FCSTD DOCUMENT  (FreeCAD 0.20R29177 +426 (Git))
Label: gearbox_00
License: Other
LicenseURL: https://www.gnu.org/licenses/gpl-3.0.en.html
objects: Part::Cylinder×128, Part::Feature×75, Part::MultiFuse×58, Part::Box×44, Part::Cut×41, Part::Chamfer×20, App::DocumentObjectGroup×9, Part::MultiCommon×7, Part::Fillet×6, Part::Part2DObjectPython×5, Part::Cone×4, Part::RegularPolygon×4, Part::Extrusion×4, Part::Compound×2
note: 398 computed .brp shape members not serialized (recipe doc carries the construction recipe); baked Part::Feature solids carry a one-line shape summary decoded from their .brp

FEATURE [Part::Box] Box377  label="Cube"
  AttacherType = Attacher::AttachEngine3D
  Height = 51
  Length = 8
  Placement = pos=(207,-16,35) rot=(0,0,1;0rad)
  Width = 32
FEATURE [Part::Box] Box761  label="Cube"
  AttacherType = Attacher::AttachEngine3D
  Height = 16
  Length = 1.5
  Placement = pos=(213,-16.25,47) rot=(0,0,1;0rad)
  Width = 10
FEATURE [Part::Box] Box762  label="Cube"
  AttacherType = Attacher::AttachEngine3D
  Height = 16
  Length = 1.5
  Placement = pos=(213,6.25,47) rot=(0,0,1;0rad)
  Width = 10
FEATURE [Part::Cylinder] Cylinder1492202  label="Cylinder"
  Angle = 360
  AttacherType = Attacher::AttachEngine3D
  FirstAngle = 0
  Height = 15.5
  Placement = pos=(199,0,55) rot=(0,1,0;1.5708rad)
  Radius = 3
  SecondAngle = 0
FEATURE [Part::Cylinder] Cylinder1492203  label="Cylinder"
  Angle = 360
  AttacherType = Attacher::AttachEngine3D
  FirstAngle = 0
  Height = 3.1
  Placement = pos=(211.4,0,55) rot=(0,1,0;1.5708rad)
  Radius = 4.6
  SecondAngle = 0
FEATURE [Part::Cylinder] Cylinder1492204  label="Cylinder"
  Angle = 360
  AttacherType = Attacher::AttachEngine3D
  FirstAngle = 0
  Height = 3.1
  Placement = pos=(206.4,0,55) rot=(0,1,0;1.5708rad)
  Radius = 4.6
  SecondAngle = 0
FEATURE [Part::Cylinder] Cylinder1492234  label="Cylinder"
  Angle = 360
  AttacherType = Attacher::AttachEngine3D
  FirstAngle = 0
  Height = 16
  Placement = pos=(211,-21,66) rot=(-1,0,0;1.5708rad)
  Radius = 1.25
  SecondAngle = 0
FEATURE [Part::Cylinder] Cylinder1492235  label="Cylinder"
  Angle = 360
  AttacherType = Attacher::AttachEngine3D
  FirstAngle = 0
  Height = 16
  Placement = pos=(211,-21,43) rot=(-1,0,0;1.5708rad)
  Radius = 1.25
  SecondAngle = 0
FEATURE [Part::Cylinder] Cylinder1492236  label="Cylinder"
  Angle = 360
  AttacherType = Attacher::AttachEngine3D
  FirstAngle = 0
  Height = 16
  Placement = pos=(211,-21,82) rot=(-1,0,0;1.5708rad)
  Radius = 1.25
  SecondAngle = 0
FEATURE [Part::Cylinder] Cylinder1492237  label="Cylinder"
  Angle = 360
  AttacherType = Attacher::AttachEngine3D
  FirstAngle = 0
  Height = 16
  Placement = pos=(211,5,66) rot=(-1,0,0;1.5708rad)
  Radius = 1.25
  SecondAngle = 0
FEATURE [Part::Cylinder] Cylinder1492238  label="Cylinder"
  Angle = 360
  AttacherType = Attacher::AttachEngine3D
  FirstAngle = 0
  Height = 16
  Placement = pos=(211,5,43) rot=(-1,0,0;1.5708rad)
  Radius = 1.25
  SecondAngle = 0
FEATURE [Part::Cylinder] Cylinder1492239  label="Cylinder"
  Angle = 360
  AttacherType = Attacher::AttachEngine3D
  FirstAngle = 0
  Height = 16
  Placement = pos=(211,5,82) rot=(-1,0,0;1.5708rad)
  Radius = 1.25
  SecondAngle = 0
FEATURE [Part::Cylinder] Cylinder1492270  label="Cylinder"
  Angle = 360
  AttacherType = Attacher::AttachEngine3D
  FirstAngle = 0
  Height = 10
  Placement = pos=(206,11.5,40) rot=(0,1,0;1.5708rad)
  Radius = 1.25
  SecondAngle = 0
FEATURE [Part::Cylinder] Cylinder1492272  label="Cylinder"
  Angle = 360
  AttacherType = Attacher::AttachEngine3D
  FirstAngle = 0
  Height = 10
  Placement = pos=(206,-11.5,40) rot=(0,1,0;1.5708rad)
  Radius = 1.25
  SecondAngle = 0
FEATURE [Part::Cylinder] Cylinder1492273  label="Cylinder"
  Angle = 360
  AttacherType = Attacher::AttachEngine3D
  FirstAngle = 0
  Height = 10
  Placement = pos=(206,-3,76) rot=(0,1,0;1.5708rad)
  Radius = 1.25
  SecondAngle = 0
FEATURE [Part::MultiFuse] Fusion004002009002027014004009002002008002004029002015013017006002012002031033002013006007008014029072011018024002019049062029014012006016002033001057009078004002010025  label="Fusion"
  Placement = pos=(0.5,0,0) rot=(0,0,1;0rad)
  Refine = true
  Shapes = -> [Cylinder1492202,Cylinder1492203,Cylinder1492204]
FEATURE [Part::Cut] Cut176013009033007019019008010045003002004008006021005004004004004002012033009016002012007022024055  label="Cut"
  Base = -> Box377
  Refine = true
  Tool = -> Fusion004002009002027014004009002002008002004029002015013017006002012002031033002013006007008014029072011018024002019049062029014012006016002033001057009078004002010025
FEATURE [Part::MultiFuse] Fusion004002009002027014004009002002008002004029002015013017006002012002031033002013006007008014029072011018024002019049062029014012006016002033001057009078004002010031010  label="Fusion"
  Placement = pos=(0.5,0,0) rot=(0,0,1;0rad)
  Refine = true
  Shapes = -> [Box762,Box761]
FEATURE [Part::Cut] Cut176013009033007019019008010045003002004008006021005004004004004002012033009016002012007022024056  label="Cut"
  Base = -> Cut176013009033007019019008010045003002004008006021005004004004004002012033009016002012007022024055
  Refine = true
  Tool = -> Fusion004002009002027014004009002002008002004029002015013017006002012002031033002013006007008014029072011018024002019049062029014012006016002033001057009078004002010031010
FEATURE [Part::MultiFuse] Fusion004002009002027014004009002002008002004029002015013017006002012002031033002013006007008014029072011018024002019049062029014012006016002033001057009078004002010031012  label="Fusion"
  Refine = true
  Shapes = -> [Cylinder1492234,Cylinder1492235,Cylinder1492236,Cylinder1492237,Cylinder1492238,Cylinder1492239]
FEATURE [Part::Cut] Cut176013009033007019019008010045003002004008006021005004004004004002012033009016002012007022024057  label="Cut"
  Base = -> Cut176013009033007019019008010045003002004008006021005004004004004002012033009016002012007022024056
  Refine = true
  Tool = -> Fusion004002009002027014004009002002008002004029002015013017006002012002031033002013006007008014029072011018024002019049062029014012006016002033001057009078004002010031012
FEATURE [Part::MultiFuse] Fusion004002009002027014004009002002008002004029002015013017006002012002031033002013006007008014029072011018024002019049062029014012006016002033001057009078004002010031016012003006  label="Fusion"
  Refine = true
  Shapes = -> [Cylinder1492270,Cylinder1492272,Cylinder1492273]
FEATURE [Part::Cut] Cut176013009033007019019008010045003002004008006010017027003005053020098001031003007007002011005005004026009003003  label="Cut"
  Base = -> Cut176013009033007019019008010045003002004008006021005004004004004002012033009016002012007022024057
  Refine = true
  Tool = -> Fusion004002009002027014004009002002008002004029002015013017006002012002031033002013006007008014029072011018024002019049062029014012006016002033001057009078004002010031016012003006
FEATURE [Part::Feature] Part__Mirroring007002003002018002002002005004004002003004003003004003001  label="diff-front-side-right-ALU5mm"
  shape: bbox 75 x 5 x 51 mm, 32 faces (baked)
FEATURE [Part::Feature] Cut176013009033007019019008010045003002004008006021005004004004004002012033009016002012007022024058001  label="diff-front-side-left-ALU5mm"
  shape: bbox 75 x 5 x 51 mm, 32 faces (baked)
FEATURE [Part::Feature] Compound003001  label="Joint"
  Placement = pos=(36,0,0) rot=(0,0,1;0rad)
  shape: bbox 25.01 x 11 x 13.99 mm, 52 faces, 2 solids (baked)
FEATURE [Part::Feature] Compound003002001  label="Joint"
  Placement = pos=(70,0,9) rot=(0,0,1;0rad)
  shape: bbox 25.01 x 11 x 13.92 mm, 52 faces, 2 solids (baked)
FEATURE [Part::Cone] Cone003  label="Cone"
  Angle = 360
  AttacherType = Attacher::AttachEngine3D
  Height = 1.5
  Placement = pos=(205.5,0,48) rot=(0,1,0;1.5708rad)
  Radius1 = 1
  Radius2 = 1.9
FEATURE [Part::Cone] Cone004  label="Cone"
  Angle = 360
  AttacherType = Attacher::AttachEngine3D
  Height = 1.5
  Placement = pos=(205.5,0,62) rot=(0,1,0;1.5708rad)
  Radius1 = 1
  Radius2 = 1.9
FEATURE [Part::Cone] Cone005  label="Cone"
  Angle = 360
  AttacherType = Attacher::AttachEngine3D
  Height = 1.5
  Placement = pos=(205.5,7,55) rot=(0,1,0;1.5708rad)
  Radius1 = 1
  Radius2 = 1.9
FEATURE [Part::Cone] Cone006  label="Cone"
  Angle = 360
  AttacherType = Attacher::AttachEngine3D
  Height = 1.5
  Placement = pos=(205.5,-7,55) rot=(0,1,0;1.5708rad)
  Radius1 = 1
  Radius2 = 1.9
FEATURE [Part::Feature] Cut176013009033007019019008010045003002004008006010017027003005053020098001031003007007002011005005004026009003002  label="BEARING-17x23x4-6703"
  Placement = pos=(264,-75,9) rot=(0,0,1;1.5708rad)
  shape: bbox 4 x 23 x 23 mm, 4 faces (baked)
FEATURE [Part::Feature] Cut176013009033007019019008010045003002004008006021005004004004004002012033009016002012007022024086  label="BEARING-5x8x2.5-MR85ZZ"
  Placement = pos=(273.5,-62,25.5) rot=(0,0,1;1.5708rad)
  shape: bbox 2.5 x 8 x 8 mm, 4 faces (baked)
FEATURE [Part::Cylinder] Cylinder1051  label="Cylinder"
  Angle = 360
  AttacherType = Attacher::AttachEngine3D
  FirstAngle = 0
  Height = 22
  Placement = pos=(118.375,0,47.903) rot=(0,1,0;1.309rad)
  Radius = 4
  SecondAngle = 0
FEATURE [Part::Cylinder] Cylinder1492252  label="Cylinder"
  Angle = 360
  AttacherType = Attacher::AttachEngine3D
  FirstAngle = 0
  Height = 10
  Placement = pos=(198,0,55) rot=(0,1,0;1.5708rad)
  Radius = 5
  SecondAngle = 0
FEATURE [Part::Cylinder] Cylinder1492253  label="Cylinder"
  Angle = 360
  AttacherType = Attacher::AttachEngine3D
  FirstAngle = 0
  Height = 48
  Placement = pos=(152,0,55) rot=(0,1,0;1.5708rad)
  Radius = 2.5
  SecondAngle = 0
FEATURE [Part::Cylinder] Cylinder1492268  label="motor"
  Angle = 360
  AttacherType = Attacher::AttachEngine3D
  FirstAngle = 0
  Height = 60
  Placement = pos=(131.5,14,77) rot=(0,1,0;1.5708rad)
  Radius = 12.5
  SecondAngle = 0
FEATURE [Part::Cylinder] Cylinder1492269  label="motor-axle"
  Angle = 360
  AttacherType = Attacher::AttachEngine3D
  FirstAngle = 0
  Height = 53
  Placement = pos=(154.5,14,77) rot=(0,1,0;1.5708rad)
  Radius = 2
  SecondAngle = 0
FEATURE [Part::Cylinder] Cylinder1492276  label="Cylinder"
  Angle = 360
  AttacherType = Attacher::AttachEngine3D
  FirstAngle = 0
  Height = 2
  Placement = pos=(205,0,55) rot=(0,1,0;1.5708rad)
  Radius = 15.5
  SecondAngle = 0
FEATURE [Part::Cylinder] Cylinder1492278  label="Cylinder"
  Angle = 360
  AttacherType = Attacher::AttachEngine3D
  FirstAngle = 0
  Height = 2
  Placement = pos=(199,0,55) rot=(0,1,0;1.5708rad)
  Radius = 11
  SecondAngle = 0
FEATURE [Part::Cylinder] Cylinder1492279  label="Cylinder"
  Angle = 360
  AttacherType = Attacher::AttachEngine3D
  FirstAngle = 0
  Height = 8
  Placement = pos=(199,0,62) rot=(0,1,0;1.5708rad)
  Radius = 1
  SecondAngle = 0
FEATURE [Part::Cylinder] Cylinder1492280  label="Cylinder"
  Angle = 360
  AttacherType = Attacher::AttachEngine3D
  FirstAngle = 0
  Height = 8
  Placement = pos=(199,0,48) rot=(0,1,0;1.5708rad)
  Radius = 1
  SecondAngle = 0
FEATURE [Part::Cylinder] Cylinder1492281  label="Cylinder"
  Angle = 360
  AttacherType = Attacher::AttachEngine3D
  FirstAngle = 0
  Height = 8
  Placement = pos=(199,7,55) rot=(0,1,0;1.5708rad)
  Radius = 1
  SecondAngle = 0
FEATURE [Part::Cylinder] Cylinder1492282  label="Cylinder"
  Angle = 360
  AttacherType = Attacher::AttachEngine3D
  FirstAngle = 0
  Height = 8
  Placement = pos=(199,-7,55) rot=(0,1,0;1.5708rad)
  Radius = 1
  SecondAngle = 0
FEATURE [Part::MultiFuse] Fusion004002009002027014004009002002008002004029002015013017006002012002031033002013006007008014029072011018024002019049062029014012006016002033001057009078004002010031016012003011  label="Fusion"
  Refine = true
  Shapes = -> [Cylinder1492279,Cylinder1492280,Cylinder1492281,Cylinder1492282,Cone003,Cone004,Cone005,Cone006]
FEATURE [Part::MultiFuse] Fusion088026007031024007008004100051055007010008005020006  label="rear-prop-shaft-STEEL"
  Refine = true
  Shapes = -> [Compound003002001,Compound003001,Cylinder1051]
FEATURE [Part::Feature] Transmission_Gear_12T_pitch214001_solid  label="Transmission_Gear_12T_pitch214"
  Placement = pos=(205,14,77) rot=(0,0,1;0rad)
  shape: bbox 10 x 16.64 x 16.64 mm, 740 faces (baked)
FEATURE [Part::MultiFuse] Fusion004002009002027014004009002002008002004029002015013017006002012002031033002013006007008014029072011018024002019049062029014012006016002033001057009078004002010031016012003004  label="GEARMOTOR"
  Placement = pos=(-0.5,-1,-5.5) rot=(0,0,1;0rad)
  Refine = true
  Shapes = -> [Cylinder1492268,Cylinder1492269,Transmission_Gear_12T_pitch214001_solid]
FEATURE [Part::Feature] Transmission_Gear_24T_pitch214001_solid  label="Transmission_Gear_24T_pitch214001 (Solid)"
  Placement = pos=(199,0,55) rot=(0,0,1;0rad)
  shape: bbox 8 x 30.9 x 30.9 mm, 1340 faces (baked)
FEATURE [Part::MultiFuse] Fusion004002009002027014004009002002008002004029002015013017006002012002031033002013006007008014029072011018024002019049062029014012006016002033001057009078004002010031016012003007  label="Fusion"
  Refine = true
  Shapes = -> [Cylinder1492276,Transmission_Gear_24T_pitch214001_solid]
FEATURE [Part::Cut] Cut176013009033007019019008010045003002004008006010017027003005053020098001031003007007002011005005004026009003004  label="Cut"
  Base = -> Fusion004002009002027014004009002002008002004029002015013017006002012002031033002013006007008014029072011018024002019049062029014012006016002033001057009078004002010031016012003007
  Refine = true
  Tool = -> Cylinder1492278
FEATURE [Part::Cut] Cut176013009033007019019008010045003002004008006010017027003005053020098001031003007007002011005005004026009003005  label="Cut"
  Base = -> Cut176013009033007019019008010045003002004008006010017027003005053020098001031003007007002011005005004026009003004
  Refine = true
  Tool = -> Cylinder1492252
FEATURE [Part::Cut] Cut176013009033007019019008010045003002004008006010017027003005053020098001031003007007002011005005004026009003009  label="gearbox-gear"
  Base = -> Cut176013009033007019019008010045003002004008006010017027003005053020098001031003007007002011005005004026009003005
  Refine = true
  Tool = -> Fusion004002009002027014004009002002008002004029002015013017006002012002031033002013006007008014029072011018024002019049062029014012006016002033001057009078004002010031016012003011
FEATURE [Part::Cylinder] Cylinder1492283  label="Cylinder"
  Angle = 360
  AttacherType = Attacher::AttachEngine3D
  FirstAngle = 0
  Height = 8
  Placement = pos=(199,0,55) rot=(0,1,0;1.5708rad)
  Radius = 5
  SecondAngle = 0
FEATURE [Part::Cylinder] Cylinder1492284  label="Cylinder"
  Angle = 360
  AttacherType = Attacher::AttachEngine3D
  FirstAngle = 0
  Height = 2
  Placement = pos=(199,0,55) rot=(0,1,0;1.5708rad)
  Radius = 11
  SecondAngle = 0
FEATURE [Part::Cylinder] Cylinder1492285  label="Cylinder"
  Angle = 360
  AttacherType = Attacher::AttachEngine3D
  FirstAngle = 0
  Height = 8
  Placement = pos=(191,0,55) rot=(0,1,0;1.5708rad)
  Radius = 8.5
  SecondAngle = 0
FEATURE [Part::Cylinder] Cylinder1492286  label="Cylinder"
  Angle = 360
  AttacherType = Attacher::AttachEngine3D
  FirstAngle = 0
  Height = 16
  Placement = pos=(191,0,55) rot=(0,1,0;1.5708rad)
  Radius = 2.5
  SecondAngle = 0
FEATURE [Part::Cylinder] Cylinder1492287  label="Cylinder"
  Angle = 360
  AttacherType = Attacher::AttachEngine3D
  FirstAngle = 0
  Height = 12
  Placement = pos=(204.5,0,49) rot=(0,1,0;0rad)
  Radius = 1
  SecondAngle = 0
FEATURE [Part::Cylinder] Cylinder1492288  label="Cylinder"
  Angle = 360
  AttacherType = Attacher::AttachEngine3D
  FirstAngle = 0
  Height = 12
  Placement = pos=(198,0,62) rot=(0,1,0;1.5708rad)
  Radius = 0.9
  SecondAngle = 0
FEATURE [Part::Cylinder] Cylinder1492289  label="Cylinder"
  Angle = 360
  AttacherType = Attacher::AttachEngine3D
  FirstAngle = 0
  Height = 12
  Placement = pos=(198,0,48) rot=(0,1,0;1.5708rad)
  Radius = 0.9
  SecondAngle = 0
FEATURE [Part::Cylinder] Cylinder1492290  label="Cylinder"
  Angle = 360
  AttacherType = Attacher::AttachEngine3D
  FirstAngle = 0
  Height = 12
  Placement = pos=(198,7,55) rot=(0,1,0;1.5708rad)
  Radius = 0.9
  SecondAngle = 0
FEATURE [Part::Cylinder] Cylinder1492291  label="Cylinder"
  Angle = 360
  AttacherType = Attacher::AttachEngine3D
  FirstAngle = 0
  Height = 12
  Placement = pos=(198,-7,55) rot=(0,1,0;1.5708rad)
  Radius = 0.9
  SecondAngle = 0
FEATURE [Part::Cylinder] Cylinder1492292  label="Cylinder"
  Angle = 360
  AttacherType = Attacher::AttachEngine3D
  FirstAngle = 0
  Height = 3
  Radius = 5.75
  SecondAngle = 0
FEATURE [Part::Cylinder] Cylinder1492293  label="Cylinder"
  Angle = 30
  AttacherType = Attacher::AttachEngine3D
  FirstAngle = 0
  Height = 3
  Placement = pos=(0,0,0) rot=(0,0,1;0.523599rad)
  Radius = 5.75
  SecondAngle = 0
FEATURE [Part::Cylinder] Cylinder1492294  label="Cylinder"
  Angle = 30
  AttacherType = Attacher::AttachEngine3D
  FirstAngle = 0
  Height = 3
  Placement = pos=(0,0,0) rot=(0,0,1;3.66519rad)
  Radius = 5.75
  SecondAngle = 0
FEATURE [Part::Cylinder] Cylinder1492295  label="Cylinder"
  Angle = 360
  AttacherType = Attacher::AttachEngine3D
  FirstAngle = 0
  Height = 3
  Radius = 5.75
  SecondAngle = 0
FEATURE [Part::Cylinder] Cylinder1492296  label="Cylinder"
  Angle = 40
  AttacherType = Attacher::AttachEngine3D
  FirstAngle = 0
  Height = 3
  Placement = pos=(0,0,0) rot=(0,0,1;0.523599rad)
  Radius = 5.75
  SecondAngle = 0
FEATURE [Part::Cylinder] Cylinder1492297  label="Cylinder"
  Angle = 40
  AttacherType = Attacher::AttachEngine3D
  FirstAngle = 0
  Height = 3
  Placement = pos=(0,0,0) rot=(0,0,1;3.66519rad)
  Radius = 5.75
  SecondAngle = 0
FEATURE [Part::Cylinder] Cylinder1492298  label="Cylinder"
  Angle = 360
  AttacherType = Attacher::AttachEngine3D
  FirstAngle = 0
  Height = 11
  Radius = 2.5
  SecondAngle = 0
FEATURE [Part::Cylinder] Cylinder1492299  label="Cylinder"
  Angle = 360
  AttacherType = Attacher::AttachEngine3D
  FirstAngle = 0
  Height = 3
  Placement = pos=(191,0,55) rot=(0,1,0;1.5708rad)
  Radius = 3
  SecondAngle = 0
FEATURE [Part::MultiFuse] Fusion004002009002027014004009002002008002004029002015013017006002012002031033002013006007008014029072011018024002019049062029014012006016002033001057009078004002010031016012003009  label="Fusion"
  Refine = true
  Shapes = -> [Cylinder1492285,Cylinder1492283,Cylinder1492284]
FEATURE [Part::Cut] Cut176013009033007019019008010045003002004008006010017027003005053020098001031003007007002011005005004026009003007  label="Cut"
  Base = -> Fusion004002009002027014004009002002008002004029002015013017006002012002031033002013006007008014029072011018024002019049062029014012006016002033001057009078004002010031016012003009
  Refine = true
  Tool = -> Cylinder1492286
FEATURE [Part::Cut] Cut176013009033007019019008010045003002004008006010017027003005053020098001031003007007002011005005004026009003008  label="Cut"
  Base = -> Cut176013009033007019019008010045003002004008006010017027003005053020098001031003007007002011005005004026009003007
  Refine = true
  Tool = -> Cylinder1492287
FEATURE [Part::MultiFuse] Fusion004002009002027014004009002002008002004029002015013017006002012002031033002013006007008014029072011018024002019049062029014012006016002033001057009078004002010031016012003010  label="Fusion"
  Placement = pos=(-3,0,0) rot=(0,0,1;0rad)
  Refine = true
  Shapes = -> [Cylinder1492288,Cylinder1492289,Cylinder1492290,Cylinder1492291]
FEATURE [Part::Cut] Cut176013009033007019019008010045003002004008006010017027003005053020098001031003007007002011005005004026009003010  label="Cut"
  Base = -> Cut176013009033007019019008010045003002004008006010017027003005053020098001031003007007002011005005004026009003008
  Refine = true
  Tool = -> Fusion004002009002027014004009002002008002004029002015013017006002012002031033002013006007008014029072011018024002019049062029014012006016002033001057009078004002010031016012003010
FEATURE [Part::MultiFuse] Fusion004002009002027014004009002002008002004029002015013017006002012002031033002013006007008014029072011018024002019049062029014012006016002033001057009078004002010031016012003012  label="Fusion"
  Refine = true
  Shapes = -> [Cylinder1492293,Cylinder1492294]
FEATURE [Part::Cut] Cut176013009033007019019008010045003002004008006010017027003005053020098001031003007007002011005005004026009003011  label="Cut"
  Base = -> Cylinder1492292
  Placement = pos=(191,0,55) rot=(0,1,0;1.5708rad)
  Refine = true
  Tool = -> Fusion004002009002027014004009002002008002004029002015013017006002012002031033002013006007008014029072011018024002019049062029014012006016002033001057009078004002010031016012003012
FEATURE [Part::Cut] Cut176013009033007019019008010045003002004008006010017027003005053020098001031003007007002011005005004026009003016  label="Cut"
  Base = -> Cut176013009033007019019008010045003002004008006010017027003005053020098001031003007007002011005005004026009003010
  Refine = true
  Tool = -> Cut176013009033007019019008010045003002004008006010017027003005053020098001031003007007002011005005004026009003011
FEATURE [Part::Cut] Cut176013009033007019019008010045003002004008006010017027003005053020098001031003007007002011005005004026009003017  label="gearbox-gear-lock-BRASS"
  Base = -> Cut176013009033007019019008010045003002004008006010017027003005053020098001031003007007002011005005004026009003016
  Refine = true
  Tool = -> Cylinder1492299
FEATURE [Part::MultiFuse] Fusion004002009002027014004009002002008002004029002015013017006002012002031033002013006007008014029072011018024002019049062029014012006016002033001057009078004002010031016012003013  label="Fusion"
  Refine = true
  Shapes = -> [Cylinder1492296,Cylinder1492297]
FEATURE [Part::Cut] Cut176013009033007019019008010045003002004008006010017027003005053020098001031003007007002011005005004026009003013  label="Cut"
  Base = -> Cylinder1492295
  Placement = pos=(0,0,0) rot=(0,0,1;0.174533rad)
  Refine = true
  Tool = -> Fusion004002009002027014004009002002008002004029002015013017006002012002031033002013006007008014029072011018024002019049062029014012006016002033001057009078004002010031016012003013
FEATURE [Part::RegularPolygon] RegularPolygon002  label="Regular polygon"
  AttacherType = Attacher::AttachEngine3D
  Circumradius = 5.75
  Polygon = 6
FEATURE [Part::Extrusion] Extrude007025
  Base = -> RegularPolygon002
  Dir = (0,0,1)
  DirMode = 2
  FaceMakerClass = Part::FaceMakerBullseye
  LengthFwd = 11
  LengthRev = 0
  Solid = true
  Symmetric = false
FEATURE [Part::Cut] Cut176013009033007019019008010045003002004008006010017027003005053020098001031003007007002011005005004026009003014  label="Cut"
  Base = -> Extrude007025
  Refine = true
  Tool = -> Cut176013009033007019019008010045003002004008006010017027003005053020098001031003007007002011005005004026009003013
FEATURE [Part::Cut] Cut176013009033007019019008010045003002004008006010017027003005053020098001031003007007002011005005004026009003015  label="Cut"
  Base = -> Cut176013009033007019019008010045003002004008006010017027003005053020098001031003007007002011005005004026009003014
  Placement = pos=(194,0,55) rot=(0,-1,0;1.5708rad)
  Refine = true
  Tool = -> Cylinder1492298
FEATURE [Part::Feature] Cut176013009033007019019008010045003002004008006021005004004004004002012033009016002012007007  label="BEARING-5x9x3-MR95ZZ"
  Placement = pos=(141,75,9) rot=(0,0,-1;1.5708rad)
  shape: bbox 3 x 9 x 9 mm, 4 faces (baked)
FEATURE [Part::Feature] Cut176013009033007019019008010045003002004008006021005004004004004002012033009016002012007006  label="BEARING-5x9x3-MR95ZZ"
  Placement = pos=(146,75,9) rot=(0,0,-1;1.5708rad)
  shape: bbox 3 x 9 x 9 mm, 4 faces (baked)
FEATURE [Part::Cylinder] Cylinder1492300  label="Cylinder"
  Angle = 360
  AttacherType = Attacher::AttachEngine3D
  FirstAngle = 0
  Height = 50
  Placement = pos=(157,11.5,40) rot=(0,1,0;1.5708rad)
  Radius = 1.5
  SecondAngle = 0
FEATURE [Part::Cylinder] Cylinder1492301  label="Cylinder"
  Angle = 360
  AttacherType = Attacher::AttachEngine3D
  FirstAngle = 0
  Height = 50
  Placement = pos=(157,-11.5,40) rot=(0,1,0;1.5708rad)
  Radius = 1.5
  SecondAngle = 0
FEATURE [Part::Cylinder] Cylinder1492302  label="Cylinder"
  Angle = 360
  AttacherType = Attacher::AttachEngine3D
  FirstAngle = 0
  Height = 50
  Placement = pos=(157,-3,76) rot=(0,1,0;1.5708rad)
  Radius = 1.5
  SecondAngle = 0
FEATURE [Part::Cylinder] Cylinder1492303  label="Cylinder"
  Angle = 360
  AttacherType = Attacher::AttachEngine3D
  FirstAngle = 0
  Height = 15
  Placement = pos=(179,0,55) rot=(0,1,0;1.5708rad)
  Radius = 3
  SecondAngle = 0
FEATURE [Part::MultiFuse] Fusion  label="gearbox-shaft-STEEL"
  Refine = true
  Shapes = -> [Cylinder1492303,Cylinder1492253]
FEATURE [Part::Cylinder] Cylinder1492304  label="Cylinder"
  Angle = 360
  AttacherType = Attacher::AttachEngine3D
  FirstAngle = 0
  Height = 2
  Placement = pos=(185.5,0,55) rot=(0,1,0;1.5708rad)
  Radius = 6
  SecondAngle = 0
FEATURE [Part::Cylinder] Cylinder1492305  label="Cylinder"
  Angle = 360
  AttacherType = Attacher::AttachEngine3D
  FirstAngle = 0
  Height = 2
  Placement = pos=(185.5,0,55) rot=(0,1,0;1.5708rad)
  Radius = 4.4
  SecondAngle = 0
FEATURE [Part::Cut] Cut
  Base = -> Cylinder1492304
  Refine = true
  Tool = -> Cylinder1492305
FEATURE [Part::Cut] Cut176013009033007019019008010045003002004008006010017027003005053020098001031003007007002011005005004026009004013003  label="gearbox-lock-STEEL"
  Base = -> Cut176013009033007019019008010045003002004008006010017027003005053020098001031003007007002011005005004026009003015
  Refine = true
  Tool = -> Cut
FEATURE [Part::Cylinder] Cylinder1492306  label="Cylinder"
  Angle = 360
  AttacherType = Attacher::AttachEngine3D
  FirstAngle = 0
  Height = 8
  Placement = pos=(207,0,55) rot=(0,-1,0;1.5708rad)
  Radius = 16
  SecondAngle = 0
FEATURE [Part::Cylinder] Cylinder1492308  label="Cylinder"
  Angle = 360
  AttacherType = Attacher::AttachEngine3D
  FirstAngle = 0
  Height = 50
  Placement = pos=(207,0,55) rot=(0,-1,0;1.5708rad)
  Radius = 4
  SecondAngle = 0
FEATURE [Part::Cylinder] Cylinder1492309  label="Cylinder"
  Angle = 360
  AttacherType = Attacher::AttachEngine3D
  FirstAngle = 0
  Height = 28
  Placement = pos=(207,0,55) rot=(0,-1,0;1.5708rad)
  Radius = 10
  SecondAngle = 0
FEATURE [Part::Cylinder] Cylinder1492310  label="Cylinder"
  Angle = 360
  AttacherType = Attacher::AttachEngine3D
  FirstAngle = 0
  Height = 3
  Placement = pos=(160,0,55) rot=(0,-1,0;1.5708rad)
  Radius = 4.6
  SecondAngle = 0
FEATURE [Part::Feature] Cut176013009033007019019008010045003002004008006021005004004004004002012033009016002012007022024016001  label="BEARING-5x9x3-MR95ZZ"
  Placement = pos=(226,-75,9) rot=(0,0,1;1.5708rad)
  shape: bbox 3 x 9 x 9 mm, 4 faces (baked)
FEATURE [Part::Feature] Cut176013009033007019019008010045003002004008006010017027003005053020098001031003007007002011005005004026009004013004  label="BEARING-5x9x3-MR95ZZ"
  Placement = pos=(245,-75,9) rot=(0,0,1;1.5708rad)
  shape: bbox 3 x 9 x 9 mm, 4 faces (baked)
FEATURE [App::DocumentObjectGroup] Group003  label="Bearings"
  Group = -> [Cut176013009033007019019008010045003002004008006021005004004004004002012033009016002012007022024086,Cut176013009033007019019008010045003002004008006010017027003005053020098001031003007007002011005005004026009003002,Cut176013009033007019019008010045003002004008006021005004004004004002012033009016002012007022024016001,+1 more]
FEATURE [Part::Cylinder] Cylinder1492311  label="Cylinder"
  Angle = 360
  AttacherType = Attacher::AttachEngine3D
  FirstAngle = 0
  Height = 3.2
  Placement = pos=(179.1,0,55) rot=(0,-1,0;1.5708rad)
  Radius = 4.6
  SecondAngle = 0
FEATURE [Part::Cylinder] Cylinder1492312  label="Cylinder"
  Angle = 360
  AttacherType = Attacher::AttachEngine3D
  FirstAngle = 0
  Height = 34
  Placement = pos=(191,13,71.5) rot=(0,-1,0;1.5708rad)
  Radius = 12.75
  SecondAngle = 0
FEATURE [Part::Cylinder] Cylinder1492313  label="Cylinder"
  Angle = 360
  AttacherType = Attacher::AttachEngine3D
  FirstAngle = 0
  Height = 2.5
  Placement = pos=(207,13,71.5) rot=(0,-1,0;1.5708rad)
  Radius = 4.1
  SecondAngle = 0
FEATURE [Part::Cylinder] Cylinder1492314  label="Cylinder"
  Angle = 360
  AttacherType = Attacher::AttachEngine3D
  FirstAngle = 0
  Height = 10.5
  Placement = pos=(204.5,13,71.5) rot=(0,-1,0;1.5708rad)
  Radius = 9.1
  SecondAngle = 0
FEATURE [Part::Cylinder] Cylinder1492315  label="Cylinder"
  Angle = 360
  AttacherType = Attacher::AttachEngine3D
  FirstAngle = 0
  Height = 8
  Placement = pos=(199,13,71.5) rot=(0,-1,0;1.5708rad)
  Radius = 6
  SecondAngle = 0
FEATURE [Part::Box] Box  label="Cube"
  AttacherType = Attacher::AttachEngine3D
  Height = 51
  Length = 32
  Placement = pos=(175,-17,35) rot=(0,0,1;0rad)
  Width = 34
FEATURE [Part::Feature] _03012_302001  label="MAGOM-PUMP"
  Placement = pos=(153,78.5,50) rot=(0.57735,-0.57735,-0.57735;2.0944rad)
  shape: bbox 115.6 x 41.21 x 42.72 mm, 1315 faces, 39 solids (baked)
FEATURE [Part::Feature] Compound003003  label="servo-DS_3218MG"
  Placement = pos=(176,-26,96) rot=(0.707107,0,-0.707107;3.14159rad)
  shape: bbox 55.85 x 47.54 x 38.43 mm, 2500 faces, 12 solids (baked)
FEATURE [Part::Cylinder] Cylinder1492316  label="Cylinder"
  Angle = 360
  AttacherType = Attacher::AttachEngine3D
  FirstAngle = 0
  Height = 72
  Placement = pos=(190,-10,55) rot=(0,-1,0;1.5708rad)
  Radius = 1.5
  SecondAngle = 0
FEATURE [Part::Feature] Cut176013009033007019019008010045003002004002002  label="rear-axle-steering-knukle-body-right"
  Placement = pos=(75,-92.5,46) rot=(0,0,1;0rad)
  shape: bbox 25.81 x 12 x 15.2 mm, 30 faces (baked)
FEATURE [Part::Feature] Cut176013009033007019019008010045003002004008006021005002002001  label="BEARING-17x23x4-6703"
  Placement = pos=(156,-75,0) rot=(0,0,1;1.5708rad)
  shape: bbox 4 x 23 x 23 mm, 4 faces (baked)
FEATURE [Part::Feature] Cut176013009033007019019008010045003002004008006021005004001001  label="BEARING-5x9x3-MR95ZZ"
  Placement = pos=(0,-24.5,0) rot=(0,0,1;0rad)
  shape: bbox 9 x 3 x 9 mm, 4 faces (baked)
FEATURE [Part::Feature] Cut176013009033007019019008010045003002004008006021005004003001  label="BEARING-5x9x3-MR95ZZ"
  Placement = pos=(0,-110.5,0) rot=(0,0,1;0rad)
  shape: bbox 9 x 3 x 9 mm, 4 faces (baked)
FEATURE [Part::Feature] Cut176013009033007019019008010045003002004008006021005004004004004002004001  label="BEARING-5x9x3-MR95ZZ"
  Placement = pos=(0,-0.5,0) rot=(0,0,1;0rad)
  shape: bbox 9 x 3 x 9 mm, 4 faces (baked)
FEATURE [Part::Feature] Cut176013009033007019019008010045003002004008006021005004004004004002005001  label="BEARING-5x9x3-MR95ZZ"
  Placement = pos=(0,-7.5,0) rot=(0,0,1;0rad)
  shape: bbox 9 x 3 x 9 mm, 4 faces (baked)
FEATURE [Part::Feature] Cut176013009033007019019008010045003002004008006021005004004004004002006001  label="BEARING-5x9x3-MR95ZZ"
  Placement = pos=(0,-134.5,0) rot=(0,0,1;0rad)
  shape: bbox 9 x 3 x 9 mm, 4 faces (baked)
FEATURE [Part::Feature] Cut176013009033007019019008010045003002004008006021005004004004004002007001  label="BEARING-5x9x3-MR95ZZ"
  Placement = pos=(0,-127.5,0) rot=(0,0,1;0rad)
  shape: bbox 9 x 3 x 9 mm, 4 faces (baked)
FEATURE [Part::Feature] Cut176013009033007019019008010045003002004008006021005004004004004002008001  label="BEARING-8x12x3.5-MR128ZZ"
  Placement = pos=(0,-77,0) rot=(0,0,1;0rad)
  shape: bbox 12 x 3.5 x 12 mm, 4 faces (baked)
FEATURE [Part::Feature] Cut176013009033007019019008010045003002004008006021005004004004004002009001  label="BEARING-5x9x3-MR95ZZ"
  Placement = pos=(163,-75,0) rot=(0,0,1;1.5708rad)
  shape: bbox 3 x 9 x 9 mm, 4 faces (baked)
FEATURE [Part::Feature] Cut176013009033007019019008010045003002004008006021005004004004004002010001  label="BEARING-5x9x3-MR95ZZ"
  Placement = pos=(158,-75,0) rot=(0,0,1;1.5708rad)
  shape: bbox 3 x 9 x 9 mm, 4 faces (baked)
FEATURE [Part::Feature] Cut176013009033007019019008010045003002004008006021005004004004004002012033009003001  label="rear-axle-pinion-side"
  shape: bbox 22 x 96 x 28 mm, 89 faces (baked)
FEATURE [Part::Feature] Cut176013009033007019019008010045003002004008006021005004004004004002012033009016002012007009001  label="BEARING-17x23x4-6703"
  Placement = pos=(127,-75,0) rot=(0,0,1;1.5708rad)
  shape: bbox 4 x 23 x 23 mm, 4 faces (baked)
FEATURE [Part::Feature] Cut176013009033007019019008010045003002004008006021005004004004004002012033009016002012007022011002  label="rear-axle-steering-knukle-lever-ALU3mm"
  shape: bbox 15.4 x 30.5 x 3 mm, 24 faces (baked)
FEATURE [Part::Feature] Cut176013009033007019019008010045003002004008006021005004004004004002012033009016002012007022024011001  label="rear-axle-front-holder-ALU5mm"
  shape: bbox 5 x 64 x 65 mm, 35 faces (baked)
FEATURE [Part::Feature] Cut176013009033007019019008010045003002004008006021005004004004004002012033009016002012007022024012001  label="rear-axle-rear-holder-ALU5mm"
  Placement = pos=(-1,0,0) rot=(0,0,1;0rad)
  shape: bbox 5 x 64 x 65 mm, 37 faces (baked)
FEATURE [Part::Feature] Cut176013009033007019019008010045003002004008006021005004004004004002012033009016002012007022024063001  label="rear-axle-knukle-holder-upper-left-ALU5mm"
  shape: bbox 14 x 24.5 x 5 mm, 23 faces (baked)
FEATURE [Part::Feature] Cut176013009033007019019008010045003002004008006021005004004004004002012033009016002012007022024068001  label="rear-axle-pump-holder-ALU5mm"
  Placement = pos=(148.844,-9e-15,0) rot=(0,0,1;3.14159rad)
  shape: bbox 25 x 34 x 5 mm, 10 faces (baked)
FEATURE [Part::Feature] Cut176013009033007019019008010045003002004008006021005004004004004002012033009016002012007022024077001  label="rear-axle-back-side"
  shape: bbox 18 x 96 x 28 mm, 101 faces (baked)
FEATURE [Part::Feature] Cut176013009033007019019008010045003002004008006021005004004004004002012033009016002012007022024081001  label="rear-axle-oscillation-limiter-10deg"
  shape: bbox 25 x 64 x 26.34 mm, 54 faces (baked)
FEATURE [Part::Feature] Cut176013009033007019019008010045003002004008006021005004004004004002012033009016002012007022024084001  label="rear-axle-attach-left-ALU6mm"
  shape: bbox 25 x 6 x 15 mm, 10 faces (baked)
FEATURE [Part::Feature] Cut176013009033007019019008010045003002004008006021005004004004004002012033009016002012007022024085001  label="rear-axle-attach-right-ALU6mm"
  shape: bbox 25 x 6 x 15 mm, 10 faces (baked)
FEATURE [Part::Feature] Cut176013009033007019019008010045003002004008006021005004004004004002012033009016002012007022025001  label="rear-axle-knukle-holder-lower-left-ALU5mm"
  shape: bbox 14 x 24.5 x 5 mm, 21 faces (baked)
FEATURE [Part::Feature] Cut176013009033007019019008010045003002004008006021005004004004008001  label="rear-axle-steering-knukle-arm-right-ALU4mm"
  Placement = pos=(75,-92.5,46) rot=(0,0,1;0rad)
  shape: bbox 24.2 x 22.25 x 4 mm, 22 faces (baked)
FEATURE [Part::Feature] Cut176013009033007019019008010045003002004008006021005005001001  label="BEARING-8x12x3.5-MR128ZZ"
  Placement = pos=(0,-57.5,0) rot=(0,0,1;0rad)
  shape: bbox 12 x 3.5 x 12 mm, 4 faces (baked)
FEATURE [Part::Feature] Cut176013009033007019019008010045003002004008006021005010001  label="wheel-axle-left"
  Placement = pos=(75,93,46) rot=(0,0,1;3.14159rad)
  shape: bbox 11 x 25 x 11 mm, 19 faces, 2 solids (baked)
FEATURE [Part::Feature] Extrude007017001  label="HEX-BAR-25mm"
  Placement = pos=(87,25,77) rot=(0,0,1;1.5708rad)
  shape: bbox 25 x 6 x 5.196 mm, 8 faces (baked)
FEATURE [Part::Feature] Extrude007018001  label="HEX-BAR-25mm"
  Placement = pos=(87,-25,77) rot=(0,0,1;1.5708rad)
  shape: bbox 25 x 6 x 5.196 mm, 8 faces (baked)
FEATURE [Part::Feature] Extrude007019001  label="HEX-BAR-25mm"
  Placement = pos=(87,21.5,64) rot=(0,0,1;1.5708rad)
  shape: bbox 25 x 6 x 5.196 mm, 8 faces (baked)
FEATURE [Part::Feature] Extrude007020001  label="HEX-BAR-25mm"
  Placement = pos=(87,-21.5,64) rot=(0,0,1;1.5708rad)
  shape: bbox 25 x 6 x 5.196 mm, 8 faces (baked)
FEATURE [Part::Feature] Fusion004002009002027014004009002002008002004029002015013017006002012002031033002013006007008014029072011018024002019049062029014012006016002033001057009067001  label="rear-axle-steering-knukle-upper-plate-right"
  shape: bbox 21.09 x 21.7 x 8.4 mm, 52 faces (baked)
FEATURE [Part::Feature] Fusion004002009002027014004009002002008002004029002015013017006002012002031033002013006007008014029072011018024002019049062029014012006016002033001057009078004002010031016012003004006002003003002005003  label="steering-link-STEEL"
  shape: bbox 101.4 x 21.08 x 15.55 mm, 9 faces (baked)
FEATURE [Part::Feature] Fusion041001001  label="differential+pinion"
  Placement = pos=(82.5,-54.5,53.5) rot=(0,1,0;3.14159rad)
  shape: bbox 40.5 x 23 x 23 mm, 14 faces (baked)
FEATURE [Part::Feature] Fusion088026007031024007008004081022014001  label="axle-shaft-left"
  Placement = pos=(75,93,46) rot=(0,0,1;3.14159rad)
  shape: bbox 6 x 53.5 x 11 mm, 15 faces (baked)
FEATURE [Part::Feature] Part__Mirroring007002003002002001  label="rear-axle-steering-knukle-body-left"
  Placement = pos=(75,93,46) rot=(0,0,1;0rad)
  shape: bbox 25.81 x 12 x 15.2 mm, 30 faces (baked)
FEATURE [Part::Feature] Part__Mirroring007002003002018002002002005001001  label="wheel-axle-right"
  shape: bbox 11 x 25 x 11 mm, 19 faces, 2 solids (baked)
FEATURE [Part::Feature] Part__Mirroring007002003002018002002002005004004002001001  label="rear-axle-knukle-holder-lower-right-ALU5mm"
  shape: bbox 14 x 24.5 x 5 mm, 21 faces (baked)
FEATURE [Part::Feature] Part__Mirroring007002003002018002002002005004004002002001  label="rear-axle-steering-knukle-upper-plate-left"
  shape: bbox 21.09 x 21.5 x 4.4 mm, 33 faces (baked)
FEATURE [Part::Feature] Part__Mirroring007002003002018002002002005004004002003001001  label="rear-axle-steering-knukle-lower-plate-left"
  Placement = pos=(0,0,92) rot=(0,0,1;0rad)
  shape: bbox 21.09 x 21.5 x 4.4 mm, 33 faces (baked)
FEATURE [Part::Feature] Part__Mirroring007002003002018002002002005004004002003002001  label="rear-axle-steering-knukle-lower-plate-right"
  Placement = pos=(0,0,92) rot=(0,0,1;0rad)
  shape: bbox 21.09 x 21.5 x 4.4 mm, 33 faces (baked)
FEATURE [Part::Feature] Part__Mirroring007002003002018002002002005004004002003003001  label="rear-axle-steering-knukle-arm-left-ALU4mm"
  shape: bbox 24.2 x 22.25 x 4 mm, 22 faces (baked)
FEATURE [Part::Feature] Part__Mirroring007002003002018002002002005004004003001  label="rear-axle-knukle-holder-upper-right-ALU5mm"
  shape: bbox 14 x 24.5 x 5 mm, 21 faces (baked)
FEATURE [Part::Feature] Part__Mirroring007002003002018002002002006001  label="axle-shaft-right"
  shape: bbox 6 x 53.5 x 11 mm, 15 faces (baked)
FEATURE [Part::Compound] Compound002005019  label="Rear-Axle"
  Links = -> [Cut176013009033007019019008010045003002004008006021005004004004004002012033009016002012007009001,Cut176013009033007019019008010045003002004008006021005004003001,Cut176013009033007019019008010045003002004008006021005004004004004002004001,Cut176013009033007019019008010045003002004008006021005004004004004002005001,Cut176013009033007019019008010045003002004008006021005004004004004002006001,+38 more]
FEATURE [App::DocumentObjectGroup] Group004  label="Rear Axle"
  Group = -> [Compound002005019]
FEATURE [Part::Cylinder] Cylinder1492317  label="Cylinder"
  Angle = 360
  AttacherType = Attacher::AttachEngine3D
  FirstAngle = 0
  Height = 2
  Placement = pos=(185.5,0,55) rot=(0,1,0;1.5708rad)
  Radius = 4.5
  SecondAngle = 0
FEATURE [Part::Box] Box763  label="Cube"
  AttacherType = Attacher::AttachEngine3D
  Height = 9
  Length = 2
  Placement = pos=(185.5,0,50.5) rot=(0,0,1;0rad)
  Width = 5
FEATURE [Part::MultiFuse] Fusion004002009002027014004009002002008002004029002015013017006002012002031033002013006007008014029072011018024002019049062029014012006016002033001057009078004002010031016012003004006002003003002005004  label="Fusion"
  Refine = true
  Shapes = -> [Box763,Cylinder1492317]
FEATURE [Part::Box] Box764  label="Cube"
  AttacherType = Attacher::AttachEngine3D
  Height = 13
  Length = 2
  Placement = pos=(185.5,-13,48.5) rot=(0,0,1;0rad)
  Width = 17
FEATURE [Part::Cut] Cut176013009033007019019008010045003002004008006010017027003005053020098001031003007007002011005005004026009004013005002002  label="Cut"
  Base = -> Box764
  Refine = true
  Tool = -> Fusion004002009002027014004009002002008002004029002015013017006002012002031033002013006007008014029072011018024002019049062029014012006016002033001057009078004002010031016012003004006002003003002005004
FEATURE [Part::Chamfer] Chamfer
  Base = -> Cut176013009033007019019008010045003002004008006010017027003005053020098001031003007007002011005005004026009004013005002002
  Edges = 2 edges: [Edge11 r1=8 r2=3.5,Edge23 r1=8 r2=3.5]
FEATURE [Part::Fillet] Fillet
  Base = -> Chamfer
  Edges = 4 edges r=4: [Edge11,Edge15,Edge19,Edge22]
FEATURE [Part::Fillet] Fillet001  label="gearbox-lock-fork"
  Base = -> Fillet
  Edges = 2 edges r=1.5: [Edge17,Edge37]
FEATURE [Part::Feature] Cut176013009033007019019008010045003002004008006010017027003005053020098001031003007007002011005005004026009004013005002003001  label="NUT-M3"
  Placement = pos=(187.5,-10,55) rot=(0,0,1;0rad)
  shape: bbox 2.5 x 5.543 x 6.4 mm, 9 faces (baked)
FEATURE [Part::Feature] Cut176013009033007019019008010045003002004008006010017027003005053020098001031003007007002011005005004026009004013005002003002  label="NUT-M3"
  Placement = pos=(183,-10,55) rot=(0,0,1;0rad)
  shape: bbox 2.5 x 5.543 x 6.4 mm, 9 faces (baked)
FEATURE [Part::MultiFuse] Fusion004002009002027014004009002002008002004029002015013017006002012002031033002013006007008014029072011018024002019049062029014012006016002033001057009078004002010031016012003004006002003003002005005  label="gearbox-lock-fork-ASSEMBLY"
  Refine = true
  Shapes = -> [Cylinder1492316,Fillet001,Cut176013009033007019019008010045003002004008006010017027003005053020098001031003007007002011005005004026009004013005002003001,Cut176013009033007019019008010045003002004008006010017027003005053020098001031003007007002011005005004026009004013005002003002]
FEATURE [Part::Cylinder] Cylinder1492318  label="Cylinder"
  Angle = 360
  AttacherType = Attacher::AttachEngine3D
  FirstAngle = 0
  Height = 22
  Placement = pos=(179,-10,55) rot=(0,-1,0;1.5708rad)
  Radius = 2
  SecondAngle = 0
FEATURE [Part::Cylinder] Cylinder1492319  label="Cylinder"
  Angle = 360
  AttacherType = Attacher::AttachEngine3D
  FirstAngle = 0
  Height = 22
  Placement = pos=(179,-10,55) rot=(0,-1,0;1.5708rad)
  Radius = 1.5
  SecondAngle = 0
FEATURE [Part::Cut] Cut176013009033007019019008010045003002004008006010017027003005053020098001031003007007002011005005004026009004013005002003003  label="gearbox-lock-fork-guide-BRASS4mm"
  Base = -> Cylinder1492318
  Refine = true
  Tool = -> Cylinder1492319
FEATURE [Part::Box] Box765  label="Cube"
  AttacherType = Attacher::AttachEngine3D
  Height = 12
  Length = 15
  Placement = pos=(179,-14,49) rot=(0,0,1;0rad)
  Width = 10
FEATURE [Part::Fillet] Fillet002
  Base = -> Box765
  Edges = 2 edges r=5: [Edge9,Edge10]
FEATURE [Part::Cylinder] Cylinder1492320  label="Cylinder"
  Angle = 360
  AttacherType = Attacher::AttachEngine3D
  FirstAngle = 0
  Height = 22
  Placement = pos=(179,-10,55) rot=(0,-1,0;1.5708rad)
  Radius = 2
  SecondAngle = 0
FEATURE [Part::Box] Box766  label="Cube"
  AttacherType = Attacher::AttachEngine3D
  Height = 28
  Length = 18
  Placement = pos=(157,-15,44) rot=(0,0,1;0rad)
  Width = 27
FEATURE [Part::Cylinder] Cylinder1492321  label="Cylinder"
  Angle = 360
  AttacherType = Attacher::AttachEngine3D
  FirstAngle = 0
  Height = 18
  Placement = pos=(157,-7,68) rot=(0,1,0;1.5708rad)
  Radius = 1.5
  SecondAngle = 0
FEATURE [Part::Cylinder] Cylinder1492322  label="Cylinder"
  Angle = 360
  AttacherType = Attacher::AttachEngine3D
  FirstAngle = 0
  Height = 26
  Placement = pos=(157,-7,68) rot=(0,1,0;1.5708rad)
  Radius = 1.25
  SecondAngle = 0
FEATURE [Part::MultiFuse] Fusion004002009002027014004009002002008002004029002015013017006002012002031033002013006007008014029072011018024002019049062029014012006016002033001057009078004002010031016012003004006002003003002005006  label="Fusion"
  Refine = true
  Shapes = -> [Cylinder1492322,Cylinder1492321]
FEATURE [Part::Cylinder] Cylinder1492323  label="Cylinder"
  Angle = 360
  AttacherType = Attacher::AttachEngine3D
  FirstAngle = 0
  Height = 18
  Placement = pos=(157,-7,68) rot=(0,1,0;1.5708rad)
  Radius = 1.5
  SecondAngle = 0
FEATURE [Part::Cylinder] Cylinder1492324  label="Cylinder"
  Angle = 360
  AttacherType = Attacher::AttachEngine3D
  FirstAngle = 0
  Height = 26
  Placement = pos=(157,-7,68) rot=(0,1,0;1.5708rad)
  Radius = 1.25
  SecondAngle = 0
FEATURE [Part::MultiFuse] Fusion004002009002027014004009002002008002004029002015013017006002012002031033002013006007008014029072011018024002019049062029014012006016002033001057009078004002010031016012003004006002003003002005007  label="Fusion"
  Placement = pos=(0,-4,-20) rot=(0,0,1;0rad)
  Refine = true
  Shapes = -> [Cylinder1492324,Cylinder1492323]
FEATURE [Part::Cylinder] Cylinder1492325  label="Cylinder"
  Angle = 360
  AttacherType = Attacher::AttachEngine3D
  FirstAngle = 0
  Height = 18
  Placement = pos=(157,-7,68) rot=(0,1,0;1.5708rad)
  Radius = 1.5
  SecondAngle = 0
FEATURE [Part::Cylinder] Cylinder1492326  label="Cylinder"
  Angle = 360
  AttacherType = Attacher::AttachEngine3D
  FirstAngle = 0
  Height = 26
  Placement = pos=(157,-7,68) rot=(0,1,0;1.5708rad)
  Radius = 1.25
  SecondAngle = 0
FEATURE [Part::MultiFuse] Fusion004002009002027014004009002002008002004029002015013017006002012002031033002013006007008014029072011018024002019049062029014012006016002033001057009078004002010031016012003004006002003003002005008  label="Fusion"
  Placement = pos=(0,15,-20) rot=(0,0,1;0rad)
  Refine = true
  Shapes = -> [Cylinder1492326,Cylinder1492325]
FEATURE [Part::MultiFuse] Fusion004002009002027014004009002002008002004029002015013017006002012002031033002013006007008014029072011018024002019049062029014012006016002033001057009078004002010031016012003004006002003003002005009  label="Fusion"
  Refine = true
  Shapes = -> [Fusion004002009002027014004009002002008002004029002015013017006002012002031033002013006007008014029072011018024002019049062029014012006016002033001057009078004002010031016012003004006002003003002005006,+2 more]
FEATURE [Part::Cylinder] Cylinder1492327  label="Cylinder"
  Angle = 360
  AttacherType = Attacher::AttachEngine3D
  FirstAngle = 0
  Height = 8
  Placement = pos=(191,13,80) rot=(0,1,0;1.5708rad)
  Radius = 1.5
  SecondAngle = 0
FEATURE [Part::Part2DObjectPython] Line022  label="gearbox-gearmotor-path"  # Draft 2D object (typed FeaturePython)
  Closed = true
  End = (272,13,71.5)
  FilletRadius = 0
  MapMode = 5
  Placement = pos=(-78,13,71.5) rot=(0,0,1;0rad)
  Points = (2) [(160,0,0),(350,0,0)]
  Start = (82,13,71.5)
FEATURE [Part::Cylinder] Cylinder1492328  label="Cylinder"
  Angle = 360
  AttacherType = Attacher::AttachEngine3D
  FirstAngle = 0
  Height = 8
  Placement = pos=(191,13,63) rot=(0,1,0;1.5708rad)
  Radius = 1.5
  SecondAngle = 0
FEATURE [App::DocumentObjectGroup] Group005  label="Joints"
  Group = -> [Line022]
FEATURE [Part::Cylinder] Cylinder1492329  label="Cylinder"
  Angle = 360
  AttacherType = Attacher::AttachEngine3D
  FirstAngle = 0
  Height = 5
  Placement = pos=(194,13,80) rot=(0,1,0;1.5708rad)
  Radius = 3
  SecondAngle = 0
FEATURE [Part::Cylinder] Cylinder1492330  label="Cylinder"
  Angle = 360
  AttacherType = Attacher::AttachEngine3D
  FirstAngle = 0
  Height = 5
  Placement = pos=(194,13,63) rot=(0,1,0;1.5708rad)
  Radius = 3
  SecondAngle = 0
FEATURE [Part::MultiFuse] Fusion004002009002027014004009002002008002004029002015013017006002012002031033002013006007008014029072011018024002019049062029014012006016002033001057009078004002010031016012003004006002003003002005012  label="Fusion"
  Refine = true
  Shapes = -> [Cylinder1492328,Cylinder1492330,Cylinder1492327,Cylinder1492329]
FEATURE [Part::Box] Box767  label="Cube"
  AttacherType = Attacher::AttachEngine3D
  Height = 30
  Length = 32
  Placement = pos=(175,-7,56) rot=(0,0,1;0rad)
  Width = 34
FEATURE [Part::Box] Box768  label="Cube"
  AttacherType = Attacher::AttachEngine3D
  Height = 30
  Length = 32
  Placement = pos=(157,-15,56) rot=(0,0,1;0rad)
  Width = 42
FEATURE [Part::Box] Box769  label="Cube"
  AttacherType = Attacher::AttachEngine3D
  Height = 20
  Length = 34
  Placement = pos=(157,-17,60) rot=(0,0,1;0rad)
  Width = 6
FEATURE [Part::Chamfer] Chamfer001
  Base = -> Box769
  Edges = 2 edges r=4: [Edge11,Edge12]
FEATURE [Part::Cylinder] Cylinder
  Angle = 360
  AttacherType = Attacher::AttachEngine3D
  FirstAngle = 0
  Height = 2
  Placement = pos=(200,27,60.5) rot=(1,0,0;1.5708rad)
  Radius = 3
  SecondAngle = 0
FEATURE [Part::MultiFuse] Fusion004002009002027014004009002002008002004029002015013017006002012002031033002013006007008014029072011018024002019049062029014012006016002033001057009078004002010031016012003015  label="gearbox-gearmotor-carvings"
  Refine = true
  Shapes = -> [Cylinder1492312,Cylinder1492313,Cylinder1492314,Cylinder1492315,Cylinder]
FEATURE [Part::Box] Box770  label="Cube"
  AttacherType = Attacher::AttachEngine3D
  Height = 51
  Length = 2.5
  Placement = pos=(204.5,-20,35) rot=(0,0,1;0rad)
  Width = 47
FEATURE [Part::Box] Box771  label="Cube"
  AttacherType = Attacher::AttachEngine3D
  Height = 71
  Length = 9
  Placement = pos=(175,-17,35) rot=(0,0,1;0rad)
  Width = 44
FEATURE [Part::Box] Box772  label="Cube"
  AttacherType = Attacher::AttachEngine3D
  Height = 51
  Length = 18
  Placement = pos=(157,-17,35) rot=(0,0,1;0rad)
  Width = 44
FEATURE [Part::Cylinder] Cylinder1492332  label="Cylinder"
  Angle = 360
  AttacherType = Attacher::AttachEngine3D
  FirstAngle = 0
  Height = 18
  Placement = pos=(157,-3,76) rot=(0,1,0;1.5708rad)
  Radius = 3.5
  SecondAngle = 0
FEATURE [Part::MultiFuse] Fusion004002009002027014004009002002008002004029002015013017006002012002031033002013006007008014029072011018024002019049062029014012006016002033001057009078004002010031016012003004006002003003002005015  label="Fusion"
  Refine = true
  Shapes = -> [Box768,Box767,Box766,Box]
FEATURE [Part::Cut] Cut176013009033007019019008010045003002004008006010017027003005053020098001031003007007002011005005004026009004013005002003004  label="Cut"
  Base = -> Fusion004002009002027014004009002002008002004029002015013017006002012002031033002013006007008014029072011018024002019049062029014012006016002033001057009078004002010031016012003004006002003003002005015
  Refine = true
  Tool = -> Chamfer001
FEATURE [Part::Fillet] Fillet003  label="Fillet"
  Base = -> Cut176013009033007019019008010045003002004008006010017027003005053020098001031003007007002011005005004026009004013005002003004
  Edges = 10 edges: [Edge7 r=4,Edge9 r=4,Edge14 r=1.5,Edge17 r=1.5,Edge19 r=6,Edge32 r=3,Edge46 r=6,Edge48 r=6,Edge49 r=5,Edge50 r=5]
FEATURE [Part::Cylinder] Cylinder1492333  label="Cylinder"
  Angle = 360
  AttacherType = Attacher::AttachEngine3D
  FirstAngle = 0
  Height = 15
  Placement = pos=(142,32,90) rot=(1,0,0;1.5708rad)
  Radius = 1.25
  SecondAngle = 0
FEATURE [Part::Feature] Fusion004002009002027014004009002002008002004029002015013017006002012002031033002013006007008014029072011018024002019049062029014012006016002033001057009078004002010031016012003004006002003003002005016  label="steering-link-STEEL"
  Placement = pos=(-12.4225,-8.36811,-1.97383) rot=(-0.005224,-0.47888,0.877865;0.054671rad)
  shape: bbox 100.2 x 25.82 x 18.05 mm, 9 faces (baked)
FEATURE [Part::Part2DObjectPython] Line025  label="rear-axle-steering-point-right"  # Draft 2D object (typed FeaturePython)
  Closed = true
  End = (62.6,-39.75,39)
  FilletRadius = 0
  MapMode = 5
  Placement = pos=(62.6,-72.25,55) rot=(0,0,1;0rad)
  Points = (2) [(0,32.5,24),(0,32.5,-16)]
  Start = (62.6,-39.75,79)
FEATURE [Part::Part2DObjectPython] Line026  label="rear-axle-steering-point-right"  # Draft 2D object (typed FeaturePython)
  Closed = true
  End = (62.6,-50,59)
  FilletRadius = 0
  MapMode = 5
  Placement = pos=(62.6,-129.5,94) rot=(0,0,1;0rad)
  Points = (2) [(0,99.5,-35),(0,79.5,-35)]
  Start = (62.6,-30,59)
FEATURE [Part::Part2DObjectPython] Line027  label="rear-axle-steering-point-right"  # Draft 2D object (typed FeaturePython)
  Closed = true
  End = (86.4,-39,39)
  FilletRadius = 0
  MapMode = 5
  Placement = pos=(86.4,-71.5,55) rot=(0,0,1;0rad)
  Points = (2) [(0,32.5,24),(0,32.5,-16)]
  Start = (86.4,-39,79)
FEATURE [Part::Part2DObjectPython] Line028  label="rear-axle-steering-point-right"  # Draft 2D object (typed FeaturePython)
  Closed = true
  End = (86.4,-50,59)
  FilletRadius = 0
  MapMode = 5
  Placement = pos=(86.4,-129.5,94) rot=(0,0,1;0rad)
  Points = (2) [(0,99.5,-35),(0,79.5,-35)]
  Start = (86.4,-30,59)
FEATURE [Part::Feature] Fusion004002009002027014004009002002008002004029002015013017006002012002031033002013006007008014029072011018024002019049062029014012006016002033001057009078004002010031016012003004006002003003002005017  label="steering-link-STEEL"
  Placement = pos=(11.5906,-7.14696,-1.97) rot=(-0.013087,-0.538001,0.842843;0.048615rad)
  shape: bbox 100.4 x 25.12 x 18.04 mm, 9 faces (baked)
FEATURE [Part::Box] Box773  label="Cube"
  AttacherType = Attacher::AttachEngine3D
  Height = 20
  Length = 7.8
  Placement = pos=(186.2,-6,86) rot=(0,0,1;0rad)
  Width = 19
FEATURE [Part::Cylinder] Cylinder1492334  label="Cylinder"
  Angle = 360
  AttacherType = Attacher::AttachEngine3D
  FirstAngle = 0
  Height = 15
  Placement = pos=(190,9,101) rot=(1,0,0;1.5708rad)
  Radius = 1.25
  SecondAngle = 0
FEATURE [Part::Cylinder] Cylinder1492335  label="Cylinder"
  Angle = 360
  AttacherType = Attacher::AttachEngine3D
  FirstAngle = 0
  Height = 15
  Placement = pos=(190,9,91) rot=(1,0,0;1.5708rad)
  Radius = 1.25
  SecondAngle = 0
FEATURE [Part::MultiFuse] Fusion004002009002027014004009002002008002004029002015013017006002012002031033002013006007008014029072011018024002019049062029014012006016002033001057009078004002010031016012003004006002003003002005018  label="Fusion"
  Refine = true
  Shapes = -> [Cylinder1492334,Cylinder1492335]
FEATURE [Part::MultiFuse] Fusion004002009002027014004009002002008002004029002015013017006002012002031033002013006007008014029072011018024002019049062029014012006016002033001057009078004002010031016012003004006002003003002005019  label="Fusion"
  Refine = true
  Shapes = -> [Fillet003,Box773]
FEATURE [Part::Cylinder] Cylinder1492338  label="Cylinder"
  Angle = 360
  AttacherType = Attacher::AttachEngine3D
  FirstAngle = 0
  Height = 15
  Placement = pos=(157,23.5,83) rot=(0,1,0;1.5708rad)
  Radius = 1.25
  SecondAngle = 0
FEATURE [Part::Cylinder] Cylinder1492339  label="Cylinder"
  Angle = 360
  AttacherType = Attacher::AttachEngine3D
  FirstAngle = 0
  Height = 15
  Placement = pos=(157,-10.5,83) rot=(0,1,0;1.5708rad)
  Radius = 1.25
  SecondAngle = 0
FEATURE [Part::MultiFuse] Fusion004002009002027014004009002002008002004029002015013017006002012002031033002013006007008014029072011018024002019049062029014012006016002033001057009078004002010031016012003004006002003003002005010  label="Fusion"
  Refine = true
  Shapes = -> [Cylinder1492300,Cylinder1492301,Cylinder1492302,Cylinder1492332,Cylinder1492338,Cylinder1492339]
FEATURE [Part::MultiFuse] Fusion004002009002027014004009002002008002004029002015013017006002012002031033002013006007008014029072011018024002019049062029014012006016002033001057009078004002010031016012003004006002003003002005011  label="gearbox-screws-carvings"
  Refine = true
  Shapes = -> [Fusion004002009002027014004009002002008002004029002015013017006002012002031033002013006007008014029072011018024002019049062029014012006016002033001057009078004002010031016012003004006002003003002005010,+3 more]
FEATURE [Part::Box] Box774  label="Cube"
  AttacherType = Attacher::AttachEngine3D
  Height = 71
  Length = 10
  Placement = pos=(184,-17,35) rot=(0,0,1;0rad)
  Width = 44
FEATURE [Part::Cylinder] Cylinder1492340  label="Cylinder"
  Angle = 360
  AttacherType = Attacher::AttachEngine3D
  FirstAngle = 0
  Height = 9
  Placement = pos=(175,8,48) rot=(0,1,0;1.5708rad)
  Radius = 3
  SecondAngle = 0
FEATURE [Part::Cut] Cut176013009033007019019008010045003002004008006010017027003005053020098001031003007007002011005005004026009004013005002003005  label="Cut"
  Base = -> Cylinder1492309
  Refine = true
  Tool = -> Cylinder1492340
FEATURE [Part::Chamfer] Chamfer002
  Base = -> Fusion004002009002027014004009002002008002004029002015013017006002012002031033002013006007008014029072011018024002019049062029014012006016002033001057009078004002010031016012003004006002003003002005019
  Edges = 1 edges: [Edge78 r1=6 r2=11]
FEATURE [Part::Cylinder] Cylinder1492341  label="Cylinder"
  Angle = 360
  AttacherType = Attacher::AttachEngine3D
  FirstAngle = 0
  Height = 13
  Placement = pos=(207,0,55) rot=(0,-1,0;1.5708rad)
  Radius = 19
  SecondAngle = 0
FEATURE [Part::MultiFuse] Fusion004002009002027014004009002002008002004029002015013017006002012002031033002013006007008014029072011018024002019049062029014012006016002033001057009078004002010031016012003004006002003003002005023  label="gearbox-base"
  Refine = true
  Shapes = -> [Chamfer002,Cylinder1492341]
FEATURE [Part::RegularPolygon] RegularPolygon004  label="Regular polygon"
  AttacherType = Attacher::AttachEngine3D
  Circumradius = 3.2
  Placement = pos=(0,0,0) rot=(0,1,0;1.5708rad)
  Polygon = 6
FEATURE [Part::Extrusion] Extrude008020
  Base = -> RegularPolygon004
  Dir = (1,0,2e-16)
  DirMode = 2
  FaceMakerClass = Part::FaceMakerBullseye
  LengthFwd = 2.5
  LengthRev = 0
  Placement = pos=(212.5,-11.5,40) rot=(0,0,1;0rad)
  Solid = true
  Symmetric = false
FEATURE [Part::RegularPolygon] RegularPolygon005  label="Regular polygon"
  AttacherType = Attacher::AttachEngine3D
  Circumradius = 3.2
  Placement = pos=(0,0,0) rot=(0,1,0;1.5708rad)
  Polygon = 6
FEATURE [Part::Extrusion] Extrude007020002
  Base = -> RegularPolygon005
  Dir = (1,0,2e-16)
  DirMode = 2
  FaceMakerClass = Part::FaceMakerBullseye
  LengthFwd = 2.5
  LengthRev = 0
  Placement = pos=(212.5,-3,76) rot=(0,0,1;0rad)
  Solid = true
  Symmetric = false
FEATURE [Part::RegularPolygon] RegularPolygon006  label="Regular polygon"
  AttacherType = Attacher::AttachEngine3D
  Circumradius = 3.2
  Placement = pos=(0,0,0) rot=(0,1,0;1.5708rad)
  Polygon = 6
FEATURE [Part::Extrusion] Extrude007020003
  Base = -> RegularPolygon006
  Dir = (1,0,2e-16)
  DirMode = 2
  FaceMakerClass = Part::FaceMakerBullseye
  LengthFwd = 2.5
  LengthRev = 0
  Placement = pos=(212.5,11.5,40) rot=(0,0,1;0rad)
  Solid = true
  Symmetric = false
FEATURE [Part::MultiFuse] Fusion004002009002027014004009002002008002004029002015013017006002012002031033002013006007008014029072011018024002019049062029014012006016002033001057009078004002010031016012003004006002003003002005024  label="Fusion"
  Refine = true
  Shapes = -> [Extrude007020003,Extrude008020,Extrude007020002]
FEATURE [Part::Cut] Cut176013009033007019019008010045003002004008006010017027003005053020098001031003007007002011005005004026009004013005002003006005  label="diff-back-side"
  Base = -> Cut176013009033007019019008010045003002004008006010017027003005053020098001031003007007002011005005004026009003003
  Refine = true
  Tool = -> Fusion004002009002027014004009002002008002004029002015013017006002012002031033002013006007008014029072011018024002019049062029014012006016002033001057009078004002010031016012003004006002003003002005024
FEATURE [App::DocumentObjectGroup] Group001  label="Front Axle"
  Group = -> [Cut176013009033007019019008010045003002004008006021005004004004004002012033009016002012007007,Cut176013009033007019019008010045003002004008006021005004004004004002012033009016002012007006,Part__Mirroring007002003002018002002002005004004002003004003003004003001,Cut176013009033007019019008010045003002004008006021005004004004004002012033009016002012007022024058001,+1 more]
FEATURE [Part::Cylinder] Cylinder1492342  label="Cylinder"
  Angle = 360
  AttacherType = Attacher::AttachEngine3D
  FirstAngle = 0
  Height = 4.3
  Placement = pos=(199,0,55) rot=(0,-1,0;1.5708rad)
  Radius = 11.6
  SecondAngle = 0
FEATURE [Part::MultiFuse] Fusion004002009002027014004009002002008002004029002015013017006002012002031033002013006007008014029072011018024002019049062029014012006016002033001057009078004002010031016012003004006002003003002005021  label="gearbox-shaft-carvings"
  Refine = true
  Shapes = -> [Cylinder1492306,Cylinder1492308,Cylinder1492310,Cylinder1492311,Fillet002,Cylinder1492320,Cut176013009033007019019008010045003002004008006010017027003005053020098001031003007007002011005005004026009004013005002003005,Cylinder1492342]
FEATURE [Part::MultiFuse] Fusion004002009002027014004009002002008002004029002015013017006002012002031033002013006007008014029072011018024002019049062029014012006016002033001057009078004002010031016012003004006002003003002005022  label="gearbox-carvings"
  Refine = true
  Shapes = -> [Fusion004002009002027014004009002002008002004029002015013017006002012002031033002013006007008014029072011018024002019049062029014012006016002033001057009078004002010031016012003015,Fusion004002009002027014004009002002008002004029002015013017006002012002031033002013006007008014029072011018024002019049062029014012006016002033001057009078004002010031016012003004006002003003002005011,+1 more]
FEATURE [Part::Cut] Cut176013009033007019019008010045003002004008006010017027003005053020098001031003007007002011005005004026009004013005002003006  label="gearbox-base-carved"
  Base = -> Fusion004002009002027014004009002002008002004029002015013017006002012002031033002013006007008014029072011018024002019049062029014012006016002033001057009078004002010031016012003004006002003003002005023
  Refine = true
  Tool = -> Fusion004002009002027014004009002002008002004029002015013017006002012002031033002013006007008014029072011018024002019049062029014012006016002033001057009078004002010031016012003004006002003003002005022
FEATURE [Part::Feature] Cut176013009033007019019008010045003002004008006010017027003005053020098001031003007007002011005005004026009004013005002003006006  label="gearbox-base-carved"
  shape: bbox 50 x 46 x 71 mm, 98 faces (baked)
FEATURE [Part::Feature] Cut176013009033007019019008010045003002004008006010017027003005053020098001031003007007002011005005004026009004013005002003006007  label="gearbox-base-carved"
  shape: bbox 50 x 46 x 71 mm, 98 faces (baked)
FEATURE [Part::Feature] Cut176013009033007019019008010045003002004008006010017027003005053020098001031003007007002011005005004026009004013005002003006008  label="gearbox-base-carved"
  shape: bbox 50 x 46 x 71 mm, 98 faces (baked)
FEATURE [Part::Feature] Cut176013009033007019019008010045003002004008006010017027003005053020098001031003007007002011005005004026009004013005002003006009  label="gearbox-base-carved"
  shape: bbox 50 x 46 x 71 mm, 98 faces (baked)
FEATURE [Part::MultiCommon] Common001  label="gearbox-cage_third_part"
  Refine = true
  Shapes = -> [Box771,Cut176013009033007019019008010045003002004008006010017027003005053020098001031003007007002011005005004026009004013005002003006007]
FEATURE [Part::MultiCommon] Common002  label="gearbox-cage_fourth_part"
  Refine = true
  Shapes = -> [Box772,Cut176013009033007019019008010045003002004008006010017027003005053020098001031003007007002011005005004026009004013005002003006008]
FEATURE [Part::MultiCommon] Common003  label="gearbox-cage_second_part"
  Refine = true
  Shapes = -> [Box774,Cut176013009033007019019008010045003002004008006010017027003005053020098001031003007007002011005005004026009004013005002003006009]
FEATURE [Part::Box] Box775  label="Cube"
  AttacherType = Attacher::AttachEngine3D
  Height = 51
  Length = 10.5
  Placement = pos=(194,-20,35) rot=(0,0,1;0rad)
  Width = 47
FEATURE [Part::Feature] Cut176013009033007019019008010045003002004008006010017027003005053020098001031003007007002011005005004026009004013005002003006010  label="gearbox-base-carved"
  shape: bbox 50 x 46 x 71 mm, 98 faces (baked)
FEATURE [Part::MultiCommon] Common  label="gearbox-cage_first_part-A"
  Refine = true
  Shapes = -> [Box770,Cut176013009033007019019008010045003002004008006010017027003005053020098001031003007007002011005005004026009004013005002003006006]
FEATURE [Part::MultiCommon] Common004  label="gearbox-cage_first_part-B"
  Refine = true
  Shapes = -> [Box775,Cut176013009033007019019008010045003002004008006010017027003005053020098001031003007007002011005005004026009004013005002003006010]
FEATURE [Part::Cylinder] Cylinder1492343  label="Cylinder"
  Angle = 360
  AttacherType = Attacher::AttachEngine3D
  FirstAngle = 0
  Height = 4.2
  Placement = pos=(199,0,55) rot=(0,-1,0;1.5708rad)
  Radius = 11.6
  SecondAngle = 0
FEATURE [Part::Cylinder] Cylinder1492344  label="Cylinder"
  Angle = 360
  AttacherType = Attacher::AttachEngine3D
  FirstAngle = 0
  Height = 5
  Placement = pos=(199,0,55) rot=(0,-1,0;1.5708rad)
  Radius = 10
  SecondAngle = 0
FEATURE [Part::Cylinder] Cylinder1492345  label="Cylinder"
  Angle = 360
  AttacherType = Attacher::AttachEngine3D
  FirstAngle = 0
  Height = 5
  Placement = pos=(199,0,55) rot=(0,-1,0;1.5708rad)
  Radius = 15.8
  SecondAngle = 0
FEATURE [Part::MultiFuse] Fusion004002009002027014004009002002008002004029002015013017006002012002031033002013006007008014029072011018024002019049062029014012006016002033001057009078004002010031016012003004006002003003002005025  label="Fusion"
  Refine = true
  Shapes = -> [Cylinder1492343,Cylinder1492344]
FEATURE [Part::Cut] Cut176013009033007019019008010045003002004008006010017027003005053020098001031003007007002011005005004026009004013005002003006011  label="Cut"
  Base = -> Cylinder1492345
  Refine = true
  Tool = -> Fusion004002009002027014004009002002008002004029002015013017006002012002031033002013006007008014029072011018024002019049062029014012006016002033001057009078004002010031016012003004006002003003002005025
FEATURE [Part::Cylinder] Cylinder1492346  label="Cylinder"
  Angle = 360
  AttacherType = Attacher::AttachEngine3D
  FirstAngle = 0
  Height = 10.5
  Placement = pos=(204.5,13,71.5) rot=(0,-1,0;1.5708rad)
  Radius = 9.1
  SecondAngle = 0
FEATURE [Part::Cylinder] Cylinder1492347  label="Cylinder"
  Angle = 360
  AttacherType = Attacher::AttachEngine3D
  FirstAngle = 0
  Height = 5
  Placement = pos=(194,13,63) rot=(0,1,0;1.5708rad)
  Radius = 3
  SecondAngle = 0
FEATURE [Part::Cylinder] Cylinder1492348  label="Cylinder"
  Angle = 360
  AttacherType = Attacher::AttachEngine3D
  FirstAngle = 0
  Height = 5
  Placement = pos=(194,13,80) rot=(0,1,0;1.5708rad)
  Radius = 3
  SecondAngle = 0
FEATURE [Part::MultiFuse] Fusion004002009002027014004009002002008002004029002015013017006002012002031033002013006007008014029072011018024002019049062029014012006016002033001057009078004002010031016012003004006002003003002005026  label="Fusion"
  Refine = true
  Shapes = -> [Cylinder1492346,Cylinder1492347,Cylinder1492348]
FEATURE [Part::Cut] Cut176013009033007019019008010045003002004008006010017027003005053020098001031003007007002011005005004026009004013005002003006012  label="Cut"
  Base = -> Cut176013009033007019019008010045003002004008006010017027003005053020098001031003007007002011005005004026009004013005002003006011
  Refine = true
  Tool = -> Fusion004002009002027014004009002002008002004029002015013017006002012002031033002013006007008014029072011018024002019049062029014012006016002033001057009078004002010031016012003004006002003003002005026
FEATURE [App::DocumentObjectGroup] Group007  label="Working"
  Group = -> [Cut176013009033007019019008010045003002004008006010017027003005053020098001031003007007002011005005004026009004013005002003006012]
FEATURE [Part::Box] Box776  label="Cube"
  AttacherType = Attacher::AttachEngine3D
  Height = 20
  Length = 7.8
  Placement = pos=(138,-6,86) rot=(0,0,1;0rad)
  Width = 33
FEATURE [Part::Cylinder] Cylinder1492349  label="Cylinder"
  Angle = 360
  AttacherType = Attacher::AttachEngine3D
  FirstAngle = 0
  Height = 15
  Placement = pos=(190,9,101) rot=(1,0,0;1.5708rad)
  Radius = 1.25
  SecondAngle = 0
FEATURE [Part::Cylinder] Cylinder1492350  label="Cylinder"
  Angle = 360
  AttacherType = Attacher::AttachEngine3D
  FirstAngle = 0
  Height = 15
  Placement = pos=(190,9,91) rot=(1,0,0;1.5708rad)
  Radius = 1.25
  SecondAngle = 0
FEATURE [Part::MultiFuse] Fusion004002009002027014004009002002008002004029002015013017006002012002031033002013006007008014029072011018024002019049062029014012006016002033001057009078004002010031016012003004006002003003002005027  label="Fusion"
  Placement = pos=(-48,0,0) rot=(0,0,1;0rad)
  Refine = true
  Shapes = -> [Cylinder1492349,Cylinder1492350]
FEATURE [Part::Box] Box777  label="Cube"
  AttacherType = Attacher::AttachEngine3D
  Height = 9
  Length = 19
  Placement = pos=(138,-15,77) rot=(0,0,1;0rad)
  Width = 42
FEATURE [Part::Cylinder] Cylinder1492351  label="Cylinder"
  Angle = 360
  AttacherType = Attacher::AttachEngine3D
  FirstAngle = 0
  Height = 25
  Placement = pos=(138,-10.5,83) rot=(0,1,0;1.5708rad)
  Radius = 1.5
  SecondAngle = 0
FEATURE [Part::Cylinder] Cylinder1492352  label="Cylinder"
  Angle = 360
  AttacherType = Attacher::AttachEngine3D
  FirstAngle = 0
  Height = 25
  Placement = pos=(138,23.5,83) rot=(0,1,0;1.5708rad)
  Radius = 1.5
  SecondAngle = 0
FEATURE [Part::Box] Box778  label="Cube"
  AttacherType = Attacher::AttachEngine3D
  Height = 10
  Length = 19
  Placement = pos=(138,22,86) rot=(0,0,1;0rad)
  Width = 5
FEATURE [Part::MultiFuse] Fusion004002009002027014004009002002008002004029002015013017006002012002031033002013006007008014029072011018024002019049062029014012006016002033001057009078004002010031016012003004006002003003002005029  label="Fusion"
  Refine = true
  Shapes = -> [Cylinder1492351,Cylinder1492352]
FEATURE [Part::Box] Box779  label="Cube"
  AttacherType = Attacher::AttachEngine3D
  Height = 9
  Length = 19
  Placement = pos=(138,-27,77) rot=(0,0,1;0rad)
  Width = 12
FEATURE [Part::Chamfer] Chamfer003
  Base = -> Box779
  Edges = 1 edges r=8: [Edge8]
FEATURE [Part::MultiFuse] Fusion004002009002027014004009002002008002004029002015013017006002012002031033002013006007008014029072011018024002019049062029014012006016002033001057009078004002010031016012003004006002003003002005030  label="Fusion"
  Refine = true
  Shapes = -> [Box776,Box777,Box778,Chamfer003]
FEATURE [Part::Chamfer] Chamfer004
  Base = -> Fusion004002009002027014004009002002008002004029002015013017006002012002031033002013006007008014029072011018024002019049062029014012006016002033001057009078004002010031016012003004006002003003002005030
  Edges = 1 edges r=3: [Edge28]
FEATURE [Part::Cylinder] Cylinder1492353  label="Cylinder"
  Angle = 360
  AttacherType = Attacher::AttachEngine3D
  FirstAngle = 0
  Height = 15
  Placement = pos=(142,-17,81.5) rot=(1,0,0;1.5708rad)
  Radius = 1.25
  SecondAngle = 0
FEATURE [Part::MultiFuse] Fusion004002009002027014004009002002008002004029002015013017006002012002031033002013006007008014029072011018024002019049062029014012006016002033001057009078004002010031016012003004006002003003002005031  label="Fusion"
  Refine = true
  Shapes = -> [Cylinder1492353,Cylinder1492333]
FEATURE [Part::MultiFuse] Fusion004002009002027014004009002002008002004029002015013017006002012002031033002013006007008014029072011018024002019049062029014012006016002033001057009078004002010031016012003004006002003003002005032  label="Fusion"
  Refine = true
  Shapes = -> [Fusion004002009002027014004009002002008002004029002015013017006002012002031033002013006007008014029072011018024002019049062029014012006016002033001057009078004002010031016012003004006002003003002005031,+2 more]
FEATURE [Part::Chamfer] Chamfer005
  Base = -> Chamfer004
  Edges = 2 edges: [Edge13 r1=10 r2=11,Edge25 r1=10 r2=15]
FEATURE [Part::Cylinder] Cylinder1492354  label="Cylinder"
  Angle = 360
  AttacherType = Attacher::AttachEngine3D
  FirstAngle = 0
  Height = 60
  Placement = pos=(191,13,71.5) rot=(0,-1,0;1.5708rad)
  Radius = 12.75
  SecondAngle = 0
FEATURE [Part::Cut] Cut176013009033007019019008010045003002004008006010017027003005053020098001031003007007002011005005004026009004013005002003006013  label="Cut"
  Base = -> Chamfer005
  Refine = true
  Tool = -> Cylinder1492354
FEATURE [Part::Cut] Cut176013009033007019019008010045003002004008006010017027003005053020098001031003007007002011005005004026009004013005002003006014  label="gearbox-servo-attach"
  Base = -> Cut176013009033007019019008010045003002004008006010017027003005053020098001031003007007002011005005004026009004013005002003006013
  Refine = true
  Tool = -> Fusion004002009002027014004009002002008002004029002015013017006002012002031033002013006007008014029072011018024002019049062029014012006016002033001057009078004002010031016012003004006002003003002005032
FEATURE [Part::Cylinder] Cylinder1492355  label="Cylinder"
  Angle = 360
  AttacherType = Attacher::AttachEngine3D
  FirstAngle = 0
  Height = 15
  Placement = pos=(142,37,90) rot=(1,0,0;1.5708rad)
  Radius = 1.5
  SecondAngle = 0
FEATURE [Part::Cylinder] Cylinder1492356  label="Cylinder"
  Angle = 360
  AttacherType = Attacher::AttachEngine3D
  FirstAngle = 0
  Height = 15
  Placement = pos=(142,-22,81.5) rot=(1,0,0;1.5708rad)
  Radius = 1.5
  SecondAngle = 0
FEATURE [Part::Box] Box780  label="Cube"
  AttacherType = Attacher::AttachEngine3D
  Height = 22
  Length = 37
  Placement = pos=(92,-32,60) rot=(0,0,1;0rad)
  Width = 32
FEATURE [Part::Chamfer] Chamfer039025078004038  label="Chamfer"
  Base = -> Box780
  Edges = 2 edges: [Edge8 r1=11 r2=36.99,Edge9 r1=21.99 r2=6.99]
FEATURE [Part::Box] Box781  label="Cube"
  AttacherType = Attacher::AttachEngine3D
  Height = 22
  Length = 37
  Placement = pos=(107,-32,69) rot=(0,0,1;0rad)
  Width = 5
FEATURE [Part::Chamfer] Chamfer039025078004039
  Base = -> Box781
  Edges = 1 edges: [Edge4 r1=14.6 r2=23.6]
FEATURE [Part::Box] Box782  label="Cube"
  AttacherType = Attacher::AttachEngine3D
  Height = 23.5
  Length = 39
  Placement = pos=(95.5,-17,59) rot=(0,0,1;0rad)
  Width = 17
FEATURE [Part::Chamfer] Chamfer039025078004040
  Base = -> Box782
  Edges = 1 edges r=5: [Edge1]
FEATURE [Part::Cylinder] Cylinder1492357  label="Cylinder"
  Angle = 360
  AttacherType = Attacher::AttachEngine3D
  FirstAngle = 0
  Height = 40
  Placement = pos=(92,0,88) rot=(0,1,0;1.5708rad)
  Radius = 18.5
  SecondAngle = 0
FEATURE [Part::Box] Box783  label="Cube"
  AttacherType = Attacher::AttachEngine3D
  Height = 11.5
  Length = 39
  Placement = pos=(95.5,-27,59) rot=(0,0,1;0rad)
  Width = 54
FEATURE [Part::Chamfer] Chamfer039025078004041
  Base = -> Box783
  Edges = 2 edges: [Edge1 r1=3 r2=33,Edge3 r1=3 r2=33]
FEATURE [Part::Box] Box784  label="Cube"
  AttacherType = Attacher::AttachEngine3D
  Height = 22
  Length = 16
  Placement = pos=(128,-32,60) rot=(0,0,1;0rad)
  Width = 32
FEATURE [Part::MultiFuse] Fusion004002009002027014004009002002008002004029002015013017006002012002031033002013006007008014029072011018024002019049062029014012006016002033001057009078004002010031016012003004006002003003002005034  label="Fusion"
  Refine = true
  Shapes = -> [Chamfer039025078004039,Box784]
FEATURE [Part::Cut] Cut176013009033007019019008010045003002004008006010017027003005053020098001031003007007002011005005004026009004013005002003006015  label="Cut"
  Base = -> Chamfer039025078004038
  Refine = true
  Tool = -> Fusion004002009002027014004009002002008002004029002015013017006002012002031033002013006007008014029072011018024002019049062029014012006016002033001057009078004002010031016012003004006002003003002005034
FEATURE [Part::Cut] Cut176013009033007019019008010045003002004008006010017027003005053020098001031003007007002011005005004026009004013005002003006016  label="Cut"
  Base = -> Cut176013009033007019019008010045003002004008006010017027003005053020098001031003007007002011005005004026009004013005002003006015
  Refine = true
  Tool = -> Chamfer039025078004040
FEATURE [Part::Feature] Part__Mirroring007002003002018002002002005004004002003004003003004003002  label="Cut"
  shape: bbox 36 x 32 x 22 mm, 13 faces (baked)
FEATURE [Part::MultiFuse] Fusion004002009002027014004009002002008002004029002015013017006002012002031033002013006007008014029072011018024002019049062029014012006016002033001057009078004002010031016012003004006002003003002005035  label="Fusion"
  Refine = true
  Shapes = -> [Cut176013009033007019019008010045003002004008006010017027003005053020098001031003007007002011005005004026009004013005002003006016,Part__Mirroring007002003002018002002002005004004002003004003003004003002]
FEATURE [Part::MultiFuse] Fusion004002009002027014004009002002008002004029002015013017006002012002031033002013006007008014029072011018024002019049062029014012006016002033001057009078004002010031016012003004006002003003002005036  label="Fusion"
  Refine = true
  Shapes = -> [Chamfer039025078004041,Cylinder1492357]
FEATURE [Part::Cut] Cut176013009033007019019008010045003002004008006010017027003005053020098001031003007007002011005005004026009004013005002003006017  label="Cut"
  Base = -> Fusion004002009002027014004009002002008002004029002015013017006002012002031033002013006007008014029072011018024002019049062029014012006016002033001057009078004002010031016012003004006002003003002005035
  Refine = true
  Tool = -> Fusion004002009002027014004009002002008002004029002015013017006002012002031033002013006007008014029072011018024002019049062029014012006016002033001057009078004002010031016012003004006002003003002005036
FEATURE [Part::Box] Box785  label="Cube"
  AttacherType = Attacher::AttachEngine3D
  Height = 12
  Length = 7.25
  Placement = pos=(92,2,58.5) rot=(0,0,1;0rad)
  Width = 22
FEATURE [Part::Box] Box786  label="Cube"
  AttacherType = Attacher::AttachEngine3D
  Height = 12
  Length = 3.5
  Placement = pos=(123.75,2,58.5) rot=(0,0,1;0rad)
  Width = 24.5
FEATURE [Part::Chamfer] Chamfer039025078004042
  Base = -> Box785
  Edges = 1 edges: [Edge11 r1=11.99 r2=14]
FEATURE [Part::Chamfer] Chamfer039025078004043
  Base = -> Box786
  Edges = 1 edges: [Edge11 r1=11.99 r2=16]
FEATURE [Part::MultiFuse] Fusion004002009002027014004009002002008002004029002015013017006002012002031033002013006007008014029072011018024002019049062029014012006016002033001057009078004002010031016012003004006002003003002005037  label="Fusion"
  Refine = true
  Shapes = -> [Cut176013009033007019019008010045003002004008006010017027003005053020098001031003007007002011005005004026009004013005002003006017,Chamfer039025078004042,Chamfer039025078004043]
FEATURE [Part::Cylinder] Cylinder1492075  label="Cylinder"
  Angle = 360
  AttacherType = Attacher::AttachEngine3D
  FirstAngle = 0
  Height = 3
  Placement = pos=(58,21.5,64) rot=(0,1,0;1.5708rad)
  Radius = 3.25
  SecondAngle = 0
FEATURE [Part::Cylinder] Cylinder1492076  label="Cylinder"
  Angle = 360
  AttacherType = Attacher::AttachEngine3D
  FirstAngle = 0
  Height = 3
  Placement = pos=(58,25,77) rot=(0,1,0;1.5708rad)
  Radius = 3.25
  SecondAngle = 0
FEATURE [Part::Cylinder] Cylinder1492077  label="Cylinder"
  Angle = 360
  AttacherType = Attacher::AttachEngine3D
  FirstAngle = 0
  Height = 3
  Placement = pos=(58,-25,77) rot=(0,1,0;1.5708rad)
  Radius = 3.25
  SecondAngle = 0
FEATURE [Part::Cylinder] Cylinder1492078  label="Cylinder"
  Angle = 360
  AttacherType = Attacher::AttachEngine3D
  FirstAngle = 0
  Height = 3
  Placement = pos=(58,-21.5,64) rot=(0,1,0;1.5708rad)
  Radius = 3.25
  SecondAngle = 0
FEATURE [Part::Cylinder] Cylinder1492133  label="Cylinder"
  Angle = 360
  AttacherType = Attacher::AttachEngine3D
  FirstAngle = 0
  Height = 3
  Placement = pos=(58,6,67) rot=(0,1,0;1.5708rad)
  Radius = 2.5
  SecondAngle = 0
FEATURE [Part::Cylinder] Cylinder1492134  label="Cylinder"
  Angle = 360
  AttacherType = Attacher::AttachEngine3D
  FirstAngle = 0
  Height = 3
  Placement = pos=(58,-6,67) rot=(0,1,0;1.5708rad)
  Radius = 2.5
  SecondAngle = 0
FEATURE [Part::MultiFuse] Fusion004002009002027014004009002002008002004029002015013017006002012002031033002013006007008014029072011018024002019049062029014012006016002033001057009048  label="Fusion"
  Refine = true
  Shapes = -> [Cylinder1492075,Cylinder1492076,Cylinder1492077,Cylinder1492078]
FEATURE [Part::MultiFuse] Fusion004002009002027014004009002002008002004029002015013017006002012002031033002013006007008014029072011018024002019049062029014012006016002033001057009072  label="Fusion"
  Refine = true
  Shapes = -> [Cylinder1492134,Cylinder1492133]
FEATURE [Part::MultiFuse] Fusion004002009002027014004009002002008002004029002015013017006002012002031033002013006007008014029072011018024002019049062029014012006016002033001057009078004002010031016012003004006002003003002005038  label="Fusion"
  Placement = pos=(34,0,0) rot=(0,0,1;0rad)
  Refine = true
  Shapes = -> [Fusion004002009002027014004009002002008002004029002015013017006002012002031033002013006007008014029072011018024002019049062029014012006016002033001057009048,Fusion004002009002027014004009002002008002004029002015013017006002012002031033002013006007008014029072011018024002019049062029014012006016002033001057009072]
FEATURE [Part::Box] Box787  label="Cube"
  AttacherType = Attacher::AttachEngine3D
  Height = 7
  Length = 33
  Placement = pos=(95,-27,82) rot=(0,0,1;0rad)
  Width = 3
FEATURE [Part::Box] Box788  label="Cube"
  AttacherType = Attacher::AttachEngine3D
  Height = 7
  Length = 33
  Placement = pos=(95,24,82) rot=(0,0,1;0rad)
  Width = 3
FEATURE [Part::Cylinder] Cylinder1492358  label="Cylinder"
  Angle = 360
  AttacherType = Attacher::AttachEngine3D
  FirstAngle = 0
  Height = 10
  Placement = pos=(125.35,12,64.5) rot=(1,0,0;1.5708rad)
  Radius = 0.9
  SecondAngle = 0
FEATURE [Part::Cylinder] Cylinder1492359  label="Cylinder"
  Angle = 360
  AttacherType = Attacher::AttachEngine3D
  FirstAngle = 0
  Height = 10
  Placement = pos=(97.75,12,64.5) rot=(1,0,0;1.5708rad)
  Radius = 0.9
  SecondAngle = 0
FEATURE [Part::Cylinder] Cylinder1492360  label="Cylinder"
  Angle = 360
  AttacherType = Attacher::AttachEngine3D
  FirstAngle = 0
  Height = 10
  Placement = pos=(100,-17,85.5) rot=(1,0,0;1.5708rad)
  Radius = 1.5
  SecondAngle = 0
FEATURE [Part::Cylinder] Cylinder1492361  label="Cylinder"
  Angle = 360
  AttacherType = Attacher::AttachEngine3D
  FirstAngle = 0
  Height = 10
  Placement = pos=(123,-17,85.5) rot=(1,0,0;1.5708rad)
  Radius = 1.5
  SecondAngle = 0
FEATURE [Part::Cylinder] Cylinder1492362  label="Cylinder"
  Angle = 360
  AttacherType = Attacher::AttachEngine3D
  FirstAngle = 0
  Height = 10
  Placement = pos=(123,27,85.5) rot=(1,0,0;1.5708rad)
  Radius = 1.5
  SecondAngle = 0
FEATURE [Part::Cylinder] Cylinder1492363  label="Cylinder"
  Angle = 360
  AttacherType = Attacher::AttachEngine3D
  FirstAngle = 0
  Height = 10
  Placement = pos=(100,27,85.5) rot=(1,0,0;1.5708rad)
  Radius = 1.5
  SecondAngle = 0
FEATURE [Part::Cylinder] Cylinder1492364  label="Cylinder"
  Angle = 360
  AttacherType = Attacher::AttachEngine3D
  FirstAngle = 0
  Height = 13
  Placement = pos=(110,20.5,70) rot=(0,0,1;1.5708rad)
  Radius = 1.5
  SecondAngle = 0
FEATURE [Part::Cylinder] Cylinder1492365  label="Cylinder"
  Angle = 360
  AttacherType = Attacher::AttachEngine3D
  FirstAngle = 0
  Height = 13
  Placement = pos=(110,-20.5,70) rot=(0,0,1;1.5708rad)
  Radius = 1.5
  SecondAngle = 0
FEATURE [Part::MultiFuse] Fusion004002009002027014004009002002008002004029002015013017006002012002031033002013006007008014029072011018024002019049062029014012006016002033001057009078004002010031016012003004006002003003002005040  label="Fusion"
  Refine = true
  Shapes = -> [Cylinder1492358,Cylinder1492359,Cylinder1492360,Cylinder1492361,Cylinder1492362,Cylinder1492363,Cylinder1492364,Cylinder1492365]
FEATURE [Part::Feature] Cut176013009033007019019008010045003002004008006010017027003005053020098001031003007007002011005005004026009004013005002003006020  label="servo-EMAX_ES08MA_II_arm"
  Placement = pos=(0,-1,0) rot=(0,1,0;0rad)
  shape: bbox 6 x 5 x 18 mm, 15 faces (baked)
FEATURE [Part::Feature] Fusion004002009002027014004009002002008002004029002015013017006002012002031033002013006007008014029072011018024002019049062029014012006016002033001057009078004002010031016012003004006002003003002005041  label="servo-EMAX_ES08MA_II"
  Placement = pos=(-5.5,-21,6) rot=(0.707107,0.707107,0;3.14159rad)
  shape: bbox 32 x 27.75 x 12 mm, 30 faces (baked)
FEATURE [Part::Compound] Compound003002002  label="servo-EMAX_ES08MA_II"
  Links = -> [Fusion004002009002027014004009002002008002004029002015013017006002012002031033002013006007008014029072011018024002019049062029014012006016002033001057009078004002010031016012003004006002003003002005041,Cut176013009033007019019008010045003002004008006010017027003005053020098001031003007007002011005005004026009004013005002003006020]
  Placement = pos=(118,-4,64.5) rot=(0,0,1;3.14159rad)
FEATURE [Part::Box] Box789  label="Cube"
  AttacherType = Attacher::AttachEngine3D
  Height = 29
  Length = 18
  Placement = pos=(128,-35,56) rot=(0,0,1;0rad)
  Width = 3
FEATURE [Part::Cylinder] Cylinder1492366  label="Cylinder"
  Angle = 360
  AttacherType = Attacher::AttachEngine3D
  FirstAngle = 0
  Height = 15
  Placement = pos=(131,-22,80.5) rot=(1,0,0;1.5708rad)
  Radius = 1.5
  SecondAngle = 0
FEATURE [Part::Cylinder] Cylinder1492367  label="Cylinder"
  Angle = 360
  AttacherType = Attacher::AttachEngine3D
  FirstAngle = 0
  Height = 15
  Placement = pos=(139,-22,60) rot=(1,0,0;1.5708rad)
  Radius = 1.5
  SecondAngle = 0
FEATURE [Part::MultiFuse] Fusion004002009002027014004009002002008002004029002015013017006002012002031033002013006007008014029072011018024002019049062029014012006016002033001057009078004002010031016012003004006002003003002005042  label="Fusion"
  Refine = true
  Shapes = -> [Cylinder1492356,Cylinder1492366,Cylinder1492367]
FEATURE [Part::Chamfer] Chamfer039025078004044
  Base = -> Box789
  Edges = 1 edges: [Edge4 r1=18 r2=7]
FEATURE [Part::Box] Box790  label="Cube"
  AttacherType = Attacher::AttachEngine3D
  Height = 38
  Length = 18
  Placement = pos=(128,-35,56) rot=(0,0,1;0rad)
  Width = 3
FEATURE [Part::Chamfer] Chamfer039025078004045
  Base = -> Box790
  Edges = 1 edges: [Edge4 r1=18 r2=7]
  Placement = pos=(0,67,0) rot=(0,0,1;0rad)
FEATURE [Part::Cylinder] Cylinder1492368  label="Cylinder"
  Angle = 360
  AttacherType = Attacher::AttachEngine3D
  FirstAngle = 0
  Height = 15
  Placement = pos=(139,37,60) rot=(1,0,0;1.5708rad)
  Radius = 1.5
  SecondAngle = 0
FEATURE [Part::Cylinder] Cylinder1492369  label="Cylinder"
  Angle = 360
  AttacherType = Attacher::AttachEngine3D
  FirstAngle = 0
  Height = 15
  Placement = pos=(131,37,80.5) rot=(1,0,0;1.5708rad)
  Radius = 1.5
  SecondAngle = 0
FEATURE [Part::Cut] Cut176013009033007019019008010045003002004008006010017027003005053020098001031003007007002011005005004026009004013005002003006021  label="gearbox-holes-right-TOOL"
  Base = -> Chamfer039025078004044
  Refine = true
  Tool = -> Fusion004002009002027014004009002002008002004029002015013017006002012002031033002013006007008014029072011018024002019049062029014012006016002033001057009078004002010031016012003004006002003003002005042
FEATURE [Part::MultiFuse] Fusion004002009002027014004009002002008002004029002015013017006002012002031033002013006007008014029072011018024002019049062029014012006016002033001057009078004002010031016012003004006002003003002005043  label="Fusion"
  Refine = true
  Shapes = -> [Cylinder1492355,Cylinder1492368,Cylinder1492369]
FEATURE [Part::Cut] Cut176013009033007019019008010045003002004008006010017027003005053020098001031003007007002011005005004026009004013005002003006022  label="gearbox-holes-left-TOOL"
  Base = -> Chamfer039025078004045
  Refine = true
  Tool = -> Fusion004002009002027014004009002002008002004029002015013017006002012002031033002013006007008014029072011018024002019049062029014012006016002033001057009078004002010031016012003004006002003003002005043
FEATURE [Part::Fillet] Fillet004
  Base = -> Fusion004002009002027014004009002002008002004029002015013017006002012002031033002013006007008014029072011018024002019049062029014012006016002033001057009078004002010031016012003004006002003003002005038
  Edges = 2 edges r=1.5: [Edge3,Edge12]
FEATURE [Part::Cut] Cut176013009033007019019008010045003002004008006010017027003005053020098001031003007007002011005005004026009004013005002003006023  label="Cut"
  Base = -> Fusion004002009002027014004009002002008002004029002015013017006002012002031033002013006007008014029072011018024002019049062029014012006016002033001057009078004002010031016012003004006002003003002005037
  Refine = true
  Tool = -> Fillet004
FEATURE [Part::MultiFuse] Fusion004002009002027014004009002002008002004029002015013017006002012002031033002013006007008014029072011018024002019049062029014012006016002033001057009078004002010031016012003004006002003003002005044  label="Fusion"
  Refine = true
  Shapes = -> [Box787,Box788,Cut176013009033007019019008010045003002004008006010017027003005053020098001031003007007002011005005004026009004013005002003006023]
FEATURE [Part::Cut] Cut176013009033007019019008010045003002004008006010017027003005053020098001031003007007002011005005004026009004013005002003006024  label="gearbox-lock-servo-mount"
  Base = -> Fusion004002009002027014004009002002008002004029002015013017006002012002031033002013006007008014029072011018024002019049062029014012006016002033001057009078004002010031016012003004006002003003002005044
  Refine = true
  Tool = -> Fusion004002009002027014004009002002008002004029002015013017006002012002031033002013006007008014029072011018024002019049062029014012006016002033001057009078004002010031016012003004006002003003002005040
FEATURE [App::DocumentObjectGroup] Group006  label="Parts"
  Group = -> [Fusion004002009002027014004009002002008002004029002015013017006002012002031033002013006007008014029072011018024002019049062029014012006016002033001057009078004002010031016012003004006002003003002005016,Line025,Line026,Line027,Line028,+3 more]
FEATURE [Part::Feature] Cut176013009033007019019008010045003002004008006010017027003005053020098001031003007007002011005005004026009004013005002003006024001  label="gearbox-lock-servo-mount"
  shape: bbox 36 x 64 x 30.5 mm, 75 faces (baked)
FEATURE [Part::Box] Box791  label="Cube"
  AttacherType = Attacher::AttachEngine3D
  Height = 29
  Length = 36
  Placement = pos=(92,24,80) rot=(0,0,1;0rad)
  Width = 8
FEATURE [Part::Feature] Cut176013009033007019019008010045003002004008006010017027003005053020098001031003007007002011005005004026009004013005002003006024003  label="gearbox-lock-servo-mount"
  shape: bbox 36 x 64 x 30.5 mm, 75 faces (baked)
FEATURE [Part::Box] Box792  label="Cube"
  AttacherType = Attacher::AttachEngine3D
  Height = 29
  Length = 36
  Placement = pos=(92,-32,80) rot=(0,0,1;0rad)
  Width = 8
FEATURE [Part::MultiCommon] Common005  label="gearbox-lock-servo-mount-left-holes-TOOL"
  Refine = true
  Shapes = -> [Cut176013009033007019019008010045003002004008006010017027003005053020098001031003007007002011005005004026009004013005002003006024001,Box791]
FEATURE [Part::MultiCommon] Common006  label="gearbox-lock-servo-mount-right-holes-TOOL"
  Refine = true
  Shapes = -> [Cut176013009033007019019008010045003002004008006010017027003005053020098001031003007007002011005005004026009004013005002003006024003,Box792]
FEATURE [App::DocumentObjectGroup] Group008  label="Tools"
  Group = -> [Cut176013009033007019019008010045003002004008006010017027003005053020098001031003007007002011005005004026009004013005002003006021,Cut176013009033007019019008010045003002004008006010017027003005053020098001031003007007002011005005004026009004013005002003006022,Common006,Common005]
FEATURE [Part::Feature] Cut176013009033007019019008010045003002004008006010017027003005053020098001031003007007002011005005004026009004013005002003006024016  label="frame-right_ALU5mm"
  shape: bbox 293 x 5 x 130 mm, 37 faces (baked)
FEATURE [Part::Feature] Cut176013009033007019019008010045003002004008006010017027003005053020098001031003007007002011005005004026009004013005002003006024015001  label="frame-left_ALU5mm"
  Placement = pos=(0,59,0) rot=(0,0,1;0rad)
  shape: bbox 293 x 5 x 130 mm, 37 faces (baked)
FEATURE [App::DocumentObjectGroup] Group  label="Frame"
  Group = -> [_03012_302001,Compound003003,Cut176013009033007019019008010045003002004008006010017027003005053020098001031003007007002011005005004026009004013005002003006024016,Cut176013009033007019019008010045003002004008006010017027003005053020098001031003007007002011005005004026009004013005002003006024015001]
FEATURE [Part::Box] Box793  label="Cube"
  AttacherType = Attacher::AttachEngine3D
  Height = 22
  Length = 37
  Placement = pos=(92,-32,60) rot=(0,0,1;0rad)
  Width = 32
FEATURE [Part::Box] Box794  label="Cube"
  AttacherType = Attacher::AttachEngine3D
  Height = 22
  Length = 37
  Placement = pos=(107,-32,69) rot=(0,0,1;0rad)
  Width = 5
FEATURE [Part::Box] Box795  label="Cube"
  AttacherType = Attacher::AttachEngine3D
  Height = 23.5
  Length = 39
  Placement = pos=(95.5,-17,59) rot=(0,0,1;0rad)
  Width = 17
FEATURE [Part::Box] Box796  label="Cube"
  AttacherType = Attacher::AttachEngine3D
  Height = 11.5
  Length = 39
  Placement = pos=(95.5,-26,59) rot=(0,0,1;0rad)
  Width = 52
FEATURE [Part::Box] Box797  label="Cube"
  AttacherType = Attacher::AttachEngine3D
  Height = 22
  Length = 16
  Placement = pos=(128,-32,60) rot=(0,0,1;0rad)
  Width = 32
FEATURE [Part::Box] Box798  label="Cube"
  AttacherType = Attacher::AttachEngine3D
  Height = 12
  Length = 7.25
  Placement = pos=(92,2,58.5) rot=(0,0,1;0rad)
  Width = 22
FEATURE [Part::Box] Box799  label="Cube"
  AttacherType = Attacher::AttachEngine3D
  Height = 12
  Length = 3.5
  Placement = pos=(123.75,2,58.5) rot=(0,0,1;0rad)
  Width = 24.5
FEATURE [Part::Box] Box800  label="Cube"
  AttacherType = Attacher::AttachEngine3D
  Height = 7
  Length = 33
  Placement = pos=(95,-27,82) rot=(0,0,1;0rad)
  Width = 3
FEATURE [Part::Box] Box801  label="Cube"
  AttacherType = Attacher::AttachEngine3D
  Height = 7
  Length = 33
  Placement = pos=(95,24,82) rot=(0,0,1;0rad)
  Width = 3
FEATURE [Part::Box] Box802  label="Cube"
  AttacherType = Attacher::AttachEngine3D
  Height = 21
  Length = 39
  Placement = pos=(92,-26.2537,60.6493) rot=(1,0,0;0.305433rad)
  Width = 2
FEATURE [Part::Chamfer] Chamfer039025078004046  label="Chamfer"
  Base = -> Box793
  Edges = 2 edges: [Edge8 r1=11 r2=36.99,Edge9 r1=21.99 r2=6.99]
FEATURE [Part::Chamfer] Chamfer039025078004047
  Base = -> Box794
  Edges = 1 edges: [Edge4 r1=14.6 r2=23.6]
FEATURE [Part::Chamfer] Chamfer039025078004048
  Base = -> Box795
  Edges = 1 edges r=5: [Edge1]
FEATURE [Part::Chamfer] Chamfer039025078004049
  Base = -> Box796
  Edges = 2 edges: [Edge1 r1=3 r2=33,Edge3 r1=3 r2=33]
FEATURE [Part::Chamfer] Chamfer039025078004050
  Base = -> Box798
  Edges = 1 edges: [Edge11 r1=11.99 r2=14]
FEATURE [Part::Chamfer] Chamfer039025078004051
  Base = -> Box799
  Edges = 1 edges: [Edge11 r1=11.99 r2=16]
FEATURE [Part::Cylinder] Cylinder1492370  label="Cylinder"
  Angle = 360
  AttacherType = Attacher::AttachEngine3D
  FirstAngle = 0
  Height = 3
  Placement = pos=(58,21.5,64) rot=(0,1,0;1.5708rad)
  Radius = 3.25
  SecondAngle = 0
FEATURE [Part::Cylinder] Cylinder1492371  label="Cylinder"
  Angle = 360
  AttacherType = Attacher::AttachEngine3D
  FirstAngle = 0
  Height = 3
  Placement = pos=(58,25,77) rot=(0,1,0;1.5708rad)
  Radius = 3.25
  SecondAngle = 0
FEATURE [Part::Cylinder] Cylinder1492372  label="Cylinder"
  Angle = 360
  AttacherType = Attacher::AttachEngine3D
  FirstAngle = 0
  Height = 3
  Placement = pos=(58,-25,77) rot=(0,1,0;1.5708rad)
  Radius = 3.25
  SecondAngle = 0
FEATURE [Part::Cylinder] Cylinder1492373  label="Cylinder"
  Angle = 360
  AttacherType = Attacher::AttachEngine3D
  FirstAngle = 0
  Height = 3
  Placement = pos=(58,-21.5,64) rot=(0,1,0;1.5708rad)
  Radius = 3.25
  SecondAngle = 0
FEATURE [Part::Cylinder] Cylinder1492374  label="Cylinder"
  Angle = 360
  AttacherType = Attacher::AttachEngine3D
  FirstAngle = 0
  Height = 3
  Placement = pos=(58,6,67) rot=(0,1,0;1.5708rad)
  Radius = 2.5
  SecondAngle = 0
FEATURE [Part::Cylinder] Cylinder1492375  label="Cylinder"
  Angle = 360
  AttacherType = Attacher::AttachEngine3D
  FirstAngle = 0
  Height = 3
  Placement = pos=(58,-6,67) rot=(0,1,0;1.5708rad)
  Radius = 2.5
  SecondAngle = 0
FEATURE [Part::Cylinder] Cylinder1492376  label="Cylinder"
  Angle = 360
  AttacherType = Attacher::AttachEngine3D
  FirstAngle = 0
  Height = 40
  Placement = pos=(92,0,88) rot=(0,1,0;1.5708rad)
  Radius = 18.5
  SecondAngle = 0
FEATURE [Part::Cylinder] Cylinder1492377  label="Cylinder"
  Angle = 360
  AttacherType = Attacher::AttachEngine3D
  FirstAngle = 0
  Height = 10
  Placement = pos=(125.35,12,64.5) rot=(1,0,0;1.5708rad)
  Radius = 0.9
  SecondAngle = 0
FEATURE [Part::Cylinder] Cylinder1492378  label="Cylinder"
  Angle = 360
  AttacherType = Attacher::AttachEngine3D
  FirstAngle = 0
  Height = 10
  Placement = pos=(97.75,12,64.5) rot=(1,0,0;1.5708rad)
  Radius = 0.9
  SecondAngle = 0
FEATURE [Part::Cylinder] Cylinder1492379  label="Cylinder"
  Angle = 360
  AttacherType = Attacher::AttachEngine3D
  FirstAngle = 0
  Height = 10
  Placement = pos=(100,-17,85.5) rot=(1,0,0;1.5708rad)
  Radius = 1.5
  SecondAngle = 0
FEATURE [Part::Cylinder] Cylinder1492380  label="Cylinder"
  Angle = 360
  AttacherType = Attacher::AttachEngine3D
  FirstAngle = 0
  Height = 10
  Placement = pos=(123,-17,85.5) rot=(1,0,0;1.5708rad)
  Radius = 1.5
  SecondAngle = 0
FEATURE [Part::Cylinder] Cylinder1492381  label="Cylinder"
  Angle = 360
  AttacherType = Attacher::AttachEngine3D
  FirstAngle = 0
  Height = 10
  Placement = pos=(123,27,85.5) rot=(1,0,0;1.5708rad)
  Radius = 1.5
  SecondAngle = 0
FEATURE [Part::Cylinder] Cylinder1492382  label="Cylinder"
  Angle = 360
  AttacherType = Attacher::AttachEngine3D
  FirstAngle = 0
  Height = 10
  Placement = pos=(100,27,85.5) rot=(1,0,0;1.5708rad)
  Radius = 1.5
  SecondAngle = 0
FEATURE [Part::Cylinder] Cylinder1492383  label="Cylinder"
  Angle = 360
  AttacherType = Attacher::AttachEngine3D
  FirstAngle = 0
  Height = 13
  Placement = pos=(110,20.5,70) rot=(0,0,1;1.5708rad)
  Radius = 1.5
  SecondAngle = 0
FEATURE [Part::Cylinder] Cylinder1492384  label="Cylinder"
  Angle = 360
  AttacherType = Attacher::AttachEngine3D
  FirstAngle = 0
  Height = 13
  Placement = pos=(110,-20.5,70) rot=(0,0,1;1.5708rad)
  Radius = 1.5
  SecondAngle = 0
FEATURE [Part::MultiFuse] Fusion004002009002027014004009002002008002004029002015013017006002012002031033002013006007008014029072011018024002019049062029014012006016002033001057009078004002010031016012003004006002003003002005025007  label="Fusion"
  Refine = true
  Shapes = -> [Cylinder1492370,Cylinder1492371,Cylinder1492372,Cylinder1492373]
FEATURE [Part::MultiFuse] Fusion004002009002027014004009002002008002004029002015013017006002012002031033002013006007008014029072011018024002019049062029014012006016002033001057009078004002010031016012003004006002003003002005025008  label="Fusion"
  Refine = true
  Shapes = -> [Cylinder1492375,Cylinder1492374]
FEATURE [Part::MultiFuse] Fusion004002009002027014004009002002008002004029002015013017006002012002031033002013006007008014029072011018024002019049062029014012006016002033001057009078004002010031016012003004006002003003002005025012  label="Fusion"
  Refine = true
  Shapes = -> [Chamfer039025078004047,Box797]
FEATURE [Part::Cut] Cut176013009033007019019008010045003002004008006010017027003005053020098001031003007007002011005005004026009004013005002003006024015002  label="Cut"
  Base = -> Chamfer039025078004046
  Refine = true
  Tool = -> Fusion004002009002027014004009002002008002004029002015013017006002012002031033002013006007008014029072011018024002019049062029014012006016002033001057009078004002010031016012003004006002003003002005025012
FEATURE [Part::Cut] Cut176013009033007019019008010045003002004008006010017027003005053020098001031003007007002011005005004026009004013005002003006024015003  label="Cut"
  Base = -> Cut176013009033007019019008010045003002004008006010017027003005053020098001031003007007002011005005004026009004013005002003006024015002
  Refine = true
  Tool = -> Chamfer039025078004048
FEATURE [Part::MultiFuse] Fusion004002009002027014004009002002008002004029002015013017006002012002031033002013006007008014029072011018024002019049062029014012006016002033001057009078004002010031016012003004006002003003002005025014  label="Fusion"
  Refine = true
  Shapes = -> [Chamfer039025078004049,Cylinder1492376]
FEATURE [Part::MultiFuse] Fusion004002009002027014004009002002008002004029002015013017006002012002031033002013006007008014029072011018024002019049062029014012006016002033001057009078004002010031016012003004006002003003002005025016  label="Fusion"
  Placement = pos=(34,0,0) rot=(0,0,1;0rad)
  Refine = true
  Shapes = -> [Fusion004002009002027014004009002002008002004029002015013017006002012002031033002013006007008014029072011018024002019049062029014012006016002033001057009078004002010031016012003004006002003003002005025007,+1 more]
FEATURE [Part::Fillet] Fillet005
  Base = -> Fusion004002009002027014004009002002008002004029002015013017006002012002031033002013006007008014029072011018024002019049062029014012006016002033001057009078004002010031016012003004006002003003002005025016
  Edges = 2 edges r=1.5: [Edge3,Edge12]
FEATURE [Part::MultiFuse] Fusion004002009002027014004009002002008002004029002015013017006002012002031033002013006007008014029072011018024002019049062029014012006016002033001057009078004002010031016012003004006002003003002005025017  label="Fusion"
  Refine = true
  Shapes = -> [Cylinder1492377,Cylinder1492378,Cylinder1492379,Cylinder1492380,Cylinder1492381,Cylinder1492382,Cylinder1492383,Cylinder1492384]
FEATURE [Part::Feature] Part__Mirroring007002003002018002002002005004004002003004003003004003004  label="Cut"
  shape: bbox 36 x 32 x 22 mm, 13 faces (baked)
FEATURE [Part::MultiFuse] Fusion004002009002027014004009002002008002004029002015013017006002012002031033002013006007008014029072011018024002019049062029014012006016002033001057009078004002010031016012003004006002003003002005025013  label="Fusion"
  Refine = true
  Shapes = -> [Cut176013009033007019019008010045003002004008006010017027003005053020098001031003007007002011005005004026009004013005002003006024015003,Part__Mirroring007002003002018002002002005004004002003004003003004003004]
FEATURE [Part::Cut] Cut176013009033007019019008010045003002004008006010017027003005053020098001031003007007002011005005004026009004013005002003006024015004  label="Cut"
  Base = -> Fusion004002009002027014004009002002008002004029002015013017006002012002031033002013006007008014029072011018024002019049062029014012006016002033001057009078004002010031016012003004006002003003002005025013
  Refine = true
  Tool = -> Fusion004002009002027014004009002002008002004029002015013017006002012002031033002013006007008014029072011018024002019049062029014012006016002033001057009078004002010031016012003004006002003003002005025014
FEATURE [Part::MultiFuse] Fusion004002009002027014004009002002008002004029002015013017006002012002031033002013006007008014029072011018024002019049062029014012006016002033001057009078004002010031016012003004006002003003002005025015  label="Fusion"
  Refine = true
  Shapes = -> [Cut176013009033007019019008010045003002004008006010017027003005053020098001031003007007002011005005004026009004013005002003006024015004,Chamfer039025078004050,Chamfer039025078004051]
FEATURE [Part::Cut] Cut176013009033007019019008010045003002004008006010017027003005053020098001031003007007002011005005004026009004013005002003006024015005  label="Cut"
  Base = -> Fusion004002009002027014004009002002008002004029002015013017006002012002031033002013006007008014029072011018024002019049062029014012006016002033001057009078004002010031016012003004006002003003002005025015
  Refine = true
  Tool = -> Fillet005
FEATURE [Part::MultiFuse] Fusion004002009002027014004009002002008002004029002015013017006002012002031033002013006007008014029072011018024002019049062029014012006016002033001057009078004002010031016012003004006002003003002005025018  label="Fusion"
  Refine = true
  Shapes = -> [Box800,Box801,Cut176013009033007019019008010045003002004008006010017027003005053020098001031003007007002011005005004026009004013005002003006024015005]
FEATURE [Part::Cut] Cut176013009033007019019008010045003002004008006010017027003005053020098001031003007007002011005005004026009004013005002003006024015006  label="gearbox-lock-servo-mount-base"
  Base = -> Fusion004002009002027014004009002002008002004029002015013017006002012002031033002013006007008014029072011018024002019049062029014012006016002033001057009078004002010031016012003004006002003003002005025018
  Refine = true
  Tool = -> Fusion004002009002027014004009002002008002004029002015013017006002012002031033002013006007008014029072011018024002019049062029014012006016002033001057009078004002010031016012003004006002003003002005025017
FEATURE [Part::Feature] Part__Mirroring007002003002018002002002005004004002003004003003004003005  label="Cube"
  shape: bbox 39 x 8.222 x 20.63 mm, 6 faces (baked)
FEATURE [Part::MultiFuse] Fusion004002009002027014004009002002008002004029002015013017006002012002031033002013006007008014029072011018024002019049062029014012006016002033001057009078004002010031016012003004006002003003002005025019  label="Fusion"
  Refine = true
  Shapes = -> [Box802,Part__Mirroring007002003002018002002002005004004002003004003003004003005]
FEATURE [Part::Cut] Cut176013009033007019019008010045003002004008006010017027003005053020098001031003007007002011005005004026009004013005002003006024015007  label="gearbox-lock-servo-mount"
  Base = -> Cut176013009033007019019008010045003002004008006010017027003005053020098001031003007007002011005005004026009004013005002003006024015006
  Refine = true
  Tool = -> Fusion004002009002027014004009002002008002004029002015013017006002012002031033002013006007008014029072011018024002019049062029014012006016002033001057009078004002010031016012003004006002003003002005025019
FEATURE [App::DocumentObjectGroup] Group002  label="Gearbox"
  Group = -> [Group003,Cut176013009033007019019008010045003002004008006010017027003005053020098001031003007007002011005005004026009003009,Fusion004002009002027014004009002002008002004029002015013017006002012002031033002013006007008014029072011018024002019049062029014012006016002033001057009078004002010031016012003004,Fusion088026007031024007008004100051055007010008005020006,+13 more]
